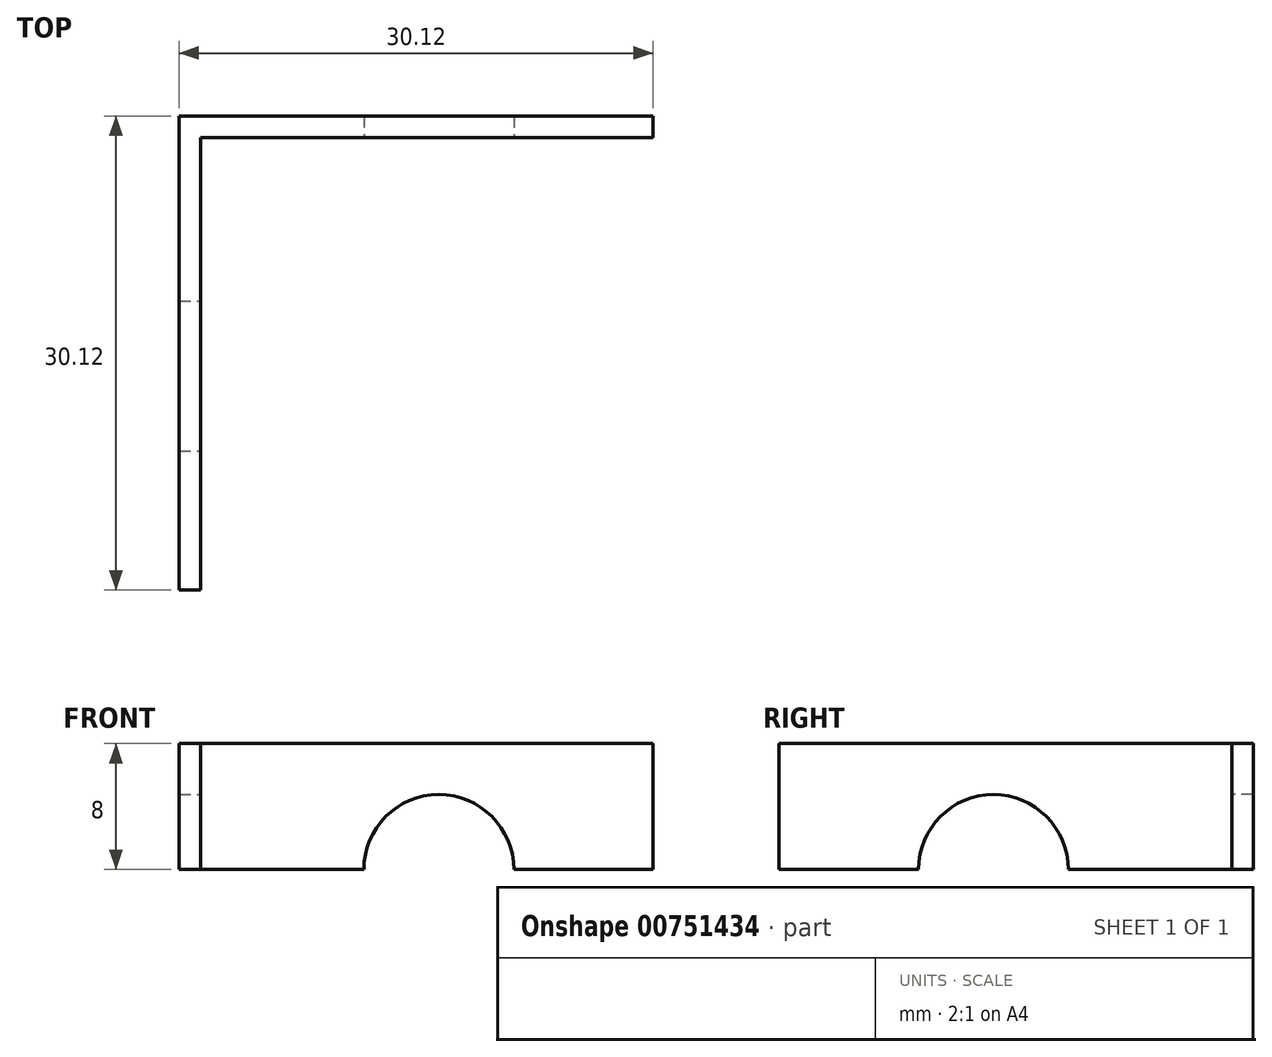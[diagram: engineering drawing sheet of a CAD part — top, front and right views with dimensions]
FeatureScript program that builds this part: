
annotation { "Feature Type Name" : "Feature", "Feature Type Description" : "" }
export const myFeature = defineFeature(function(context is Context, id is Id, definition is map)
    precondition{}
    {
        {
            assignVariable(context, id + "F0", {"name" : "height", "anyValue" : 8});
        }
        {
            var Q0;
            Q0=qCreatedBy(makeId("Top.planeOp"),FACE);
            var sketch = newSketch(context, id + "F1", { "sketchPlane" : qUnion([Q0])});
            skLineSegment(sketch, "E0", {"start": v(-1.37, -28.75) * mm, "end": v(-1.37, 1.37) * mm});
            skLineSegment(sketch, "E1", {"start": v(-1.37, 1.37) * mm, "end": v(28.75, 1.37) * mm});
            skLineSegment(sketch, "E2", {"start": v(28.75, 1.37) * mm, "end": v(28.75, 0) * mm});
            skLineSegment(sketch, "E3", {"start": v(28.75, 0) * mm, "end": v(0, 0) * mm});
            skLineSegment(sketch, "E4", {"start": v(0, 0) * mm, "end": v(0, -28.75) * mm});
            skLineSegment(sketch, "E5", {"start": v(0, -28.75) * mm, "end": v(-1.37, -28.75) * mm});
            skSolve(sketch);
        }
        {
            var Q0;
            Q0=makeQuery(id+"F1.imprint","IMPRINT",FACE,{"disambiguationData":[TD([[makeQuery(id+"F1.imprint","IMPRINT",EDGE,{"derivedFrom":sQuery(id+"F1.wireOp",EDGE,"E0")}),-1.0]])]});
            extrude(context, id + "F2", {"entities" : qUnion([Q0]), "depth" : (getVariable(context, 'height')) * mm, "offsetDistance" : 25.4 * mm});
        }
        {
            var Q0;
            Q0=makeQuery(id+"F2.opExtrude","SWEPT_FACE",FACE,{"disambiguationData":[OSD([sQuery(id+"F1.wireOp",EDGE,"E3")])]});
            var sketch = newSketch(context, id + "F3", { "sketchPlane" : qUnion([Q0])});
            skPoint(sketch, "E6", {"position": v(15.14, 19.05) * mm});
            skLineSegment(sketch, "E7", {"start": v(15.14, 0) * mm, "end": v(15.14, 203.2) * mm, "construction": true});
            skCircle(sketch, "E8", {"center": v(15.14, 19.05) * mm, "radius": 4.76 * mm});
            skCircle(sketch, "E9", {"center": v(15.14, 0) * mm, "radius": 4.76 * mm});
            skPoint(sketch, "E10", {"position": v(15.14, 38.1) * mm});
            skPoint(sketch, "E11", {"position": v(15.14, 57.15) * mm});
            skArc(sketch, "E12", {"start": v(19.9, 39.69) * mm, "mid": v(15.14, 44.45) * mm, "end": v(10.38, 39.69) * mm});
            skArc(sketch, "E13", {"start": v(10.38, 36.51) * mm, "mid": v(15.14, 31.75) * mm, "end": v(19.9, 36.51) * mm});
            skLineSegment(sketch, "E14", {"start": v(19.9, 39.69) * mm, "end": v(19.9, 36.51) * mm});
            skLineSegment(sketch, "E15", {"start": v(10.38, 39.69) * mm, "end": v(10.38, 36.51) * mm});
            skArc(sketch, "E16", {"start": v(19.9, 58.74) * mm, "mid": v(15.14, 63.5) * mm, "end": v(10.38, 58.74) * mm});
            skArc(sketch, "E17", {"start": v(10.38, 55.56) * mm, "mid": v(15.14, 50.8) * mm, "end": v(19.9, 55.56) * mm});
            skLineSegment(sketch, "E18", {"start": v(19.9, 58.74) * mm, "end": v(19.9, 55.56) * mm});
            skLineSegment(sketch, "E19", {"start": v(10.38, 58.74) * mm, "end": v(10.38, 55.56) * mm});
            skPoint(sketch, "E20.0.1.0", {"position": v(15.14, 133.35) * mm});
            skArc(sketch, "E20.0.1.1", {"start": v(19.9, 134.94) * mm, "mid": v(15.14, 139.7) * mm, "end": v(10.38, 134.94) * mm});
            skPoint(sketch, "E20.0.1.2", {"position": v(15.14, 114.3) * mm});
            skPoint(sketch, "E20.0.1.3", {"position": v(15.14, 95.25) * mm});
            skArc(sketch, "E20.0.1.4", {"start": v(10.38, 131.76) * mm, "mid": v(15.14, 127) * mm, "end": v(19.9, 131.76) * mm});
            skCircle(sketch, "E20.0.1.5", {"center": v(15.14, 95.25) * mm, "radius": 4.76 * mm});
            skCircle(sketch, "E20.0.1.6", {"center": v(15.14, 76.2) * mm, "radius": 4.76 * mm});
            skArc(sketch, "E20.0.1.7", {"start": v(19.9, 115.89) * mm, "mid": v(15.14, 120.65) * mm, "end": v(10.38, 115.89) * mm});
            skArc(sketch, "E20.0.1.8", {"start": v(10.38, 112.71) * mm, "mid": v(15.14, 107.95) * mm, "end": v(19.9, 112.71) * mm});
            skPoint(sketch, "E20.0.1.9", {"position": v(15.14, 133.35) * mm});
            skPoint(sketch, "E20.0.1.10", {"position": v(15.14, 114.3) * mm});
            skLineSegment(sketch, "E20.0.1.11", {"start": v(10.38, 134.94) * mm, "end": v(10.38, 131.76) * mm});
            skLineSegment(sketch, "E20.0.1.12", {"start": v(19.9, 134.94) * mm, "end": v(19.9, 131.76) * mm});
            skLineSegment(sketch, "E20.0.1.13", {"start": v(19.9, 115.89) * mm, "end": v(19.9, 112.71) * mm});
            skLineSegment(sketch, "E20.0.1.14", {"start": v(10.38, 115.89) * mm, "end": v(10.38, 112.71) * mm});
            skPoint(sketch, "E20.0.2.0", {"position": v(15.14, 209.55) * mm});
            skArc(sketch, "E20.0.2.1", {"start": v(19.9, 211.14) * mm, "mid": v(15.14, 215.9) * mm, "end": v(10.38, 211.14) * mm});
            skPoint(sketch, "E20.0.2.2", {"position": v(15.14, 190.5) * mm});
            skPoint(sketch, "E20.0.2.3", {"position": v(15.14, 171.45) * mm});
            skArc(sketch, "E20.0.2.4", {"start": v(10.38, 207.96) * mm, "mid": v(15.14, 203.2) * mm, "end": v(19.9, 207.96) * mm});
            skCircle(sketch, "E20.0.2.5", {"center": v(15.14, 171.45) * mm, "radius": 4.76 * mm});
            skCircle(sketch, "E20.0.2.6", {"center": v(15.14, 152.4) * mm, "radius": 4.76 * mm});
            skArc(sketch, "E20.0.2.7", {"start": v(19.9, 192.09) * mm, "mid": v(15.14, 196.85) * mm, "end": v(10.38, 192.09) * mm});
            skArc(sketch, "E20.0.2.8", {"start": v(10.38, 188.91) * mm, "mid": v(15.14, 184.15) * mm, "end": v(19.9, 188.91) * mm});
            skPoint(sketch, "E20.0.2.9", {"position": v(15.14, 209.55) * mm});
            skPoint(sketch, "E20.0.2.10", {"position": v(15.14, 190.5) * mm});
            skLineSegment(sketch, "E20.0.2.11", {"start": v(10.38, 211.14) * mm, "end": v(10.38, 207.96) * mm});
            skLineSegment(sketch, "E20.0.2.12", {"start": v(19.9, 211.14) * mm, "end": v(19.9, 207.96) * mm});
            skLineSegment(sketch, "E20.0.2.13", {"start": v(19.9, 192.09) * mm, "end": v(19.9, 188.91) * mm});
            skLineSegment(sketch, "E20.0.2.14", {"start": v(10.38, 192.09) * mm, "end": v(10.38, 188.91) * mm});
            skPoint(sketch, "E20.0.3.0", {"position": v(15.14, 285.75) * mm});
            skArc(sketch, "E20.0.3.1", {"start": v(19.9, 287.34) * mm, "mid": v(15.14, 292.1) * mm, "end": v(10.38, 287.34) * mm});
            skPoint(sketch, "E20.0.3.2", {"position": v(15.14, 266.7) * mm});
            skPoint(sketch, "E20.0.3.3", {"position": v(15.14, 247.65) * mm});
            skArc(sketch, "E20.0.3.4", {"start": v(10.38, 284.16) * mm, "mid": v(15.14, 279.4) * mm, "end": v(19.9, 284.16) * mm});
            skCircle(sketch, "E20.0.3.5", {"center": v(15.14, 247.65) * mm, "radius": 4.76 * mm});
            skCircle(sketch, "E20.0.3.6", {"center": v(15.14, 228.6) * mm, "radius": 4.76 * mm});
            skArc(sketch, "E20.0.3.7", {"start": v(19.9, 268.29) * mm, "mid": v(15.14, 273.05) * mm, "end": v(10.38, 268.29) * mm});
            skArc(sketch, "E20.0.3.8", {"start": v(10.38, 265.11) * mm, "mid": v(15.14, 260.35) * mm, "end": v(19.9, 265.11) * mm});
            skPoint(sketch, "E20.0.3.9", {"position": v(15.14, 285.75) * mm});
            skPoint(sketch, "E20.0.3.10", {"position": v(15.14, 266.7) * mm});
            skLineSegment(sketch, "E20.0.3.11", {"start": v(10.38, 287.34) * mm, "end": v(10.38, 284.16) * mm});
            skLineSegment(sketch, "E20.0.3.12", {"start": v(19.9, 287.34) * mm, "end": v(19.9, 284.16) * mm});
            skLineSegment(sketch, "E20.0.3.13", {"start": v(19.9, 268.29) * mm, "end": v(19.9, 265.11) * mm});
            skLineSegment(sketch, "E20.0.3.14", {"start": v(10.38, 268.29) * mm, "end": v(10.38, 265.11) * mm});
            skPoint(sketch, "E20.0.4.0", {"position": v(15.14, 361.95) * mm});
            skArc(sketch, "E20.0.4.1", {"start": v(19.9, 363.54) * mm, "mid": v(15.14, 368.3) * mm, "end": v(10.38, 363.54) * mm});
            skPoint(sketch, "E20.0.4.2", {"position": v(15.14, 342.9) * mm});
            skPoint(sketch, "E20.0.4.3", {"position": v(15.14, 323.85) * mm});
            skArc(sketch, "E20.0.4.4", {"start": v(10.38, 360.36) * mm, "mid": v(15.14, 355.6) * mm, "end": v(19.9, 360.36) * mm});
            skCircle(sketch, "E20.0.4.5", {"center": v(15.14, 323.85) * mm, "radius": 4.76 * mm});
            skCircle(sketch, "E20.0.4.6", {"center": v(15.14, 304.8) * mm, "radius": 4.76 * mm});
            skArc(sketch, "E20.0.4.7", {"start": v(19.9, 344.49) * mm, "mid": v(15.14, 349.25) * mm, "end": v(10.38, 344.49) * mm});
            skArc(sketch, "E20.0.4.8", {"start": v(10.38, 341.31) * mm, "mid": v(15.14, 336.55) * mm, "end": v(19.9, 341.31) * mm});
            skPoint(sketch, "E20.0.4.9", {"position": v(15.14, 361.95) * mm});
            skPoint(sketch, "E20.0.4.10", {"position": v(15.14, 342.9) * mm});
            skLineSegment(sketch, "E20.0.4.11", {"start": v(10.38, 363.54) * mm, "end": v(10.38, 360.36) * mm});
            skLineSegment(sketch, "E20.0.4.12", {"start": v(19.9, 363.54) * mm, "end": v(19.9, 360.36) * mm});
            skLineSegment(sketch, "E20.0.4.13", {"start": v(19.9, 344.49) * mm, "end": v(19.9, 341.31) * mm});
            skLineSegment(sketch, "E20.0.4.14", {"start": v(10.38, 344.49) * mm, "end": v(10.38, 341.31) * mm});
            skPoint(sketch, "E20.0.5.0", {"position": v(15.14, 438.15) * mm});
            skArc(sketch, "E20.0.5.1", {"start": v(19.9, 439.74) * mm, "mid": v(15.14, 444.5) * mm, "end": v(10.38, 439.74) * mm});
            skPoint(sketch, "E20.0.5.2", {"position": v(15.14, 419.1) * mm});
            skPoint(sketch, "E20.0.5.3", {"position": v(15.14, 400.05) * mm});
            skArc(sketch, "E20.0.5.4", {"start": v(10.38, 436.56) * mm, "mid": v(15.14, 431.8) * mm, "end": v(19.9, 436.56) * mm});
            skCircle(sketch, "E20.0.5.5", {"center": v(15.14, 400.05) * mm, "radius": 4.76 * mm});
            skCircle(sketch, "E20.0.5.6", {"center": v(15.14, 381) * mm, "radius": 4.76 * mm});
            skArc(sketch, "E20.0.5.7", {"start": v(19.9, 420.69) * mm, "mid": v(15.14, 425.45) * mm, "end": v(10.38, 420.69) * mm});
            skArc(sketch, "E20.0.5.8", {"start": v(10.38, 417.51) * mm, "mid": v(15.14, 412.75) * mm, "end": v(19.9, 417.51) * mm});
            skPoint(sketch, "E20.0.5.9", {"position": v(15.14, 438.15) * mm});
            skPoint(sketch, "E20.0.5.10", {"position": v(15.14, 419.1) * mm});
            skLineSegment(sketch, "E20.0.5.11", {"start": v(10.38, 439.74) * mm, "end": v(10.38, 436.56) * mm});
            skLineSegment(sketch, "E20.0.5.12", {"start": v(19.9, 439.74) * mm, "end": v(19.9, 436.56) * mm});
            skLineSegment(sketch, "E20.0.5.13", {"start": v(19.9, 420.69) * mm, "end": v(19.9, 417.51) * mm});
            skLineSegment(sketch, "E20.0.5.14", {"start": v(10.38, 420.69) * mm, "end": v(10.38, 417.51) * mm});
            skPoint(sketch, "E20.0.6.0", {"position": v(15.14, 514.35) * mm});
            skArc(sketch, "E20.0.6.1", {"start": v(19.9, 515.94) * mm, "mid": v(15.14, 520.7) * mm, "end": v(10.38, 515.94) * mm});
            skPoint(sketch, "E20.0.6.2", {"position": v(15.14, 495.3) * mm});
            skPoint(sketch, "E20.0.6.3", {"position": v(15.14, 476.25) * mm});
            skArc(sketch, "E20.0.6.4", {"start": v(10.38, 512.76) * mm, "mid": v(15.14, 508) * mm, "end": v(19.9, 512.76) * mm});
            skCircle(sketch, "E20.0.6.5", {"center": v(15.14, 476.25) * mm, "radius": 4.76 * mm});
            skCircle(sketch, "E20.0.6.6", {"center": v(15.14, 457.2) * mm, "radius": 4.76 * mm});
            skArc(sketch, "E20.0.6.7", {"start": v(19.9, 496.89) * mm, "mid": v(15.14, 501.65) * mm, "end": v(10.38, 496.89) * mm});
            skArc(sketch, "E20.0.6.8", {"start": v(10.38, 493.71) * mm, "mid": v(15.14, 488.95) * mm, "end": v(19.9, 493.71) * mm});
            skPoint(sketch, "E20.0.6.9", {"position": v(15.14, 514.35) * mm});
            skPoint(sketch, "E20.0.6.10", {"position": v(15.14, 495.3) * mm});
            skLineSegment(sketch, "E20.0.6.11", {"start": v(10.38, 515.94) * mm, "end": v(10.38, 512.76) * mm});
            skLineSegment(sketch, "E20.0.6.12", {"start": v(19.9, 515.94) * mm, "end": v(19.9, 512.76) * mm});
            skLineSegment(sketch, "E20.0.6.13", {"start": v(19.9, 496.89) * mm, "end": v(19.9, 493.71) * mm});
            skLineSegment(sketch, "E20.0.6.14", {"start": v(10.38, 496.89) * mm, "end": v(10.38, 493.71) * mm});
            skPoint(sketch, "E20.0.7.0", {"position": v(15.14, 590.55) * mm});
            skArc(sketch, "E20.0.7.1", {"start": v(19.9, 592.14) * mm, "mid": v(15.14, 596.9) * mm, "end": v(10.38, 592.14) * mm});
            skPoint(sketch, "E20.0.7.2", {"position": v(15.14, 571.5) * mm});
            skPoint(sketch, "E20.0.7.3", {"position": v(15.14, 552.45) * mm});
            skArc(sketch, "E20.0.7.4", {"start": v(10.38, 588.96) * mm, "mid": v(15.14, 584.2) * mm, "end": v(19.9, 588.96) * mm});
            skCircle(sketch, "E20.0.7.5", {"center": v(15.14, 552.45) * mm, "radius": 4.76 * mm});
            skCircle(sketch, "E20.0.7.6", {"center": v(15.14, 533.4) * mm, "radius": 4.76 * mm});
            skArc(sketch, "E20.0.7.7", {"start": v(19.9, 573.09) * mm, "mid": v(15.14, 577.85) * mm, "end": v(10.38, 573.09) * mm});
            skArc(sketch, "E20.0.7.8", {"start": v(10.38, 569.91) * mm, "mid": v(15.14, 565.15) * mm, "end": v(19.9, 569.91) * mm});
            skPoint(sketch, "E20.0.7.9", {"position": v(15.14, 590.55) * mm});
            skPoint(sketch, "E20.0.7.10", {"position": v(15.14, 571.5) * mm});
            skLineSegment(sketch, "E20.0.7.11", {"start": v(10.38, 592.14) * mm, "end": v(10.38, 588.96) * mm});
            skLineSegment(sketch, "E20.0.7.12", {"start": v(19.9, 592.14) * mm, "end": v(19.9, 588.96) * mm});
            skLineSegment(sketch, "E20.0.7.13", {"start": v(19.9, 573.09) * mm, "end": v(19.9, 569.91) * mm});
            skLineSegment(sketch, "E20.0.7.14", {"start": v(10.38, 573.09) * mm, "end": v(10.38, 569.91) * mm});
            skPoint(sketch, "E20.0.8.0", {"position": v(15.14, 666.75) * mm});
            skArc(sketch, "E20.0.8.1", {"start": v(19.9, 668.34) * mm, "mid": v(15.14, 673.1) * mm, "end": v(10.38, 668.34) * mm});
            skPoint(sketch, "E20.0.8.2", {"position": v(15.14, 647.7) * mm});
            skPoint(sketch, "E20.0.8.3", {"position": v(15.14, 628.65) * mm});
            skArc(sketch, "E20.0.8.4", {"start": v(10.38, 665.16) * mm, "mid": v(15.14, 660.4) * mm, "end": v(19.9, 665.16) * mm});
            skCircle(sketch, "E20.0.8.5", {"center": v(15.14, 628.65) * mm, "radius": 4.76 * mm});
            skCircle(sketch, "E20.0.8.6", {"center": v(15.14, 609.6) * mm, "radius": 4.76 * mm});
            skArc(sketch, "E20.0.8.7", {"start": v(19.9, 649.29) * mm, "mid": v(15.14, 654.05) * mm, "end": v(10.38, 649.29) * mm});
            skArc(sketch, "E20.0.8.8", {"start": v(10.38, 646.11) * mm, "mid": v(15.14, 641.35) * mm, "end": v(19.9, 646.11) * mm});
            skPoint(sketch, "E20.0.8.9", {"position": v(15.14, 666.75) * mm});
            skPoint(sketch, "E20.0.8.10", {"position": v(15.14, 647.7) * mm});
            skLineSegment(sketch, "E20.0.8.11", {"start": v(10.38, 668.34) * mm, "end": v(10.38, 665.16) * mm});
            skLineSegment(sketch, "E20.0.8.12", {"start": v(19.9, 668.34) * mm, "end": v(19.9, 665.16) * mm});
            skLineSegment(sketch, "E20.0.8.13", {"start": v(19.9, 649.29) * mm, "end": v(19.9, 646.11) * mm});
            skLineSegment(sketch, "E20.0.8.14", {"start": v(10.38, 649.29) * mm, "end": v(10.38, 646.11) * mm});
            skPoint(sketch, "E20.0.9.0", {"position": v(15.14, 742.95) * mm});
            skArc(sketch, "E20.0.9.1", {"start": v(19.9, 744.54) * mm, "mid": v(15.14, 749.3) * mm, "end": v(10.38, 744.54) * mm});
            skPoint(sketch, "E20.0.9.2", {"position": v(15.14, 723.9) * mm});
            skPoint(sketch, "E20.0.9.3", {"position": v(15.14, 704.85) * mm});
            skArc(sketch, "E20.0.9.4", {"start": v(10.38, 741.36) * mm, "mid": v(15.14, 736.6) * mm, "end": v(19.9, 741.36) * mm});
            skCircle(sketch, "E20.0.9.5", {"center": v(15.14, 704.85) * mm, "radius": 4.76 * mm});
            skCircle(sketch, "E20.0.9.6", {"center": v(15.14, 685.8) * mm, "radius": 4.76 * mm});
            skArc(sketch, "E20.0.9.7", {"start": v(19.9, 725.49) * mm, "mid": v(15.14, 730.25) * mm, "end": v(10.38, 725.49) * mm});
            skArc(sketch, "E20.0.9.8", {"start": v(10.38, 722.31) * mm, "mid": v(15.14, 717.55) * mm, "end": v(19.9, 722.31) * mm});
            skPoint(sketch, "E20.0.9.9", {"position": v(15.14, 742.95) * mm});
            skPoint(sketch, "E20.0.9.10", {"position": v(15.14, 723.9) * mm});
            skLineSegment(sketch, "E20.0.9.11", {"start": v(10.38, 744.54) * mm, "end": v(10.38, 741.36) * mm});
            skLineSegment(sketch, "E20.0.9.12", {"start": v(19.9, 744.54) * mm, "end": v(19.9, 741.36) * mm});
            skLineSegment(sketch, "E20.0.9.13", {"start": v(19.9, 725.49) * mm, "end": v(19.9, 722.31) * mm});
            skLineSegment(sketch, "E20.0.9.14", {"start": v(10.38, 725.49) * mm, "end": v(10.38, 722.31) * mm});
            skPoint(sketch, "E20.0.10.0", {"position": v(15.14, 819.15) * mm});
            skArc(sketch, "E20.0.10.1", {"start": v(19.9, 820.74) * mm, "mid": v(15.14, 825.5) * mm, "end": v(10.38, 820.74) * mm});
            skPoint(sketch, "E20.0.10.2", {"position": v(15.14, 800.1) * mm});
            skPoint(sketch, "E20.0.10.3", {"position": v(15.14, 781.05) * mm});
            skArc(sketch, "E20.0.10.4", {"start": v(10.38, 817.56) * mm, "mid": v(15.14, 812.8) * mm, "end": v(19.9, 817.56) * mm});
            skCircle(sketch, "E20.0.10.5", {"center": v(15.14, 781.05) * mm, "radius": 4.76 * mm});
            skCircle(sketch, "E20.0.10.6", {"center": v(15.14, 762) * mm, "radius": 4.76 * mm});
            skArc(sketch, "E20.0.10.7", {"start": v(19.9, 801.69) * mm, "mid": v(15.14, 806.45) * mm, "end": v(10.38, 801.69) * mm});
            skArc(sketch, "E20.0.10.8", {"start": v(10.38, 798.51) * mm, "mid": v(15.14, 793.75) * mm, "end": v(19.9, 798.51) * mm});
            skPoint(sketch, "E20.0.10.9", {"position": v(15.14, 819.15) * mm});
            skPoint(sketch, "E20.0.10.10", {"position": v(15.14, 800.1) * mm});
            skLineSegment(sketch, "E20.0.10.11", {"start": v(10.38, 820.74) * mm, "end": v(10.38, 817.56) * mm});
            skLineSegment(sketch, "E20.0.10.12", {"start": v(19.9, 820.74) * mm, "end": v(19.9, 817.56) * mm});
            skLineSegment(sketch, "E20.0.10.13", {"start": v(19.9, 801.69) * mm, "end": v(19.9, 798.51) * mm});
            skLineSegment(sketch, "E20.0.10.14", {"start": v(10.38, 801.69) * mm, "end": v(10.38, 798.51) * mm});
            skPoint(sketch, "E20.0.11.0", {"position": v(15.14, 895.35) * mm});
            skArc(sketch, "E20.0.11.1", {"start": v(19.9, 896.94) * mm, "mid": v(15.14, 901.7) * mm, "end": v(10.38, 896.94) * mm});
            skPoint(sketch, "E20.0.11.2", {"position": v(15.14, 876.3) * mm});
            skPoint(sketch, "E20.0.11.3", {"position": v(15.14, 857.25) * mm});
            skArc(sketch, "E20.0.11.4", {"start": v(10.38, 893.76) * mm, "mid": v(15.14, 889) * mm, "end": v(19.9, 893.76) * mm});
            skCircle(sketch, "E20.0.11.5", {"center": v(15.14, 857.25) * mm, "radius": 4.76 * mm});
            skCircle(sketch, "E20.0.11.6", {"center": v(15.14, 838.2) * mm, "radius": 4.76 * mm});
            skArc(sketch, "E20.0.11.7", {"start": v(19.9, 877.89) * mm, "mid": v(15.14, 882.65) * mm, "end": v(10.38, 877.89) * mm});
            skArc(sketch, "E20.0.11.8", {"start": v(10.38, 874.71) * mm, "mid": v(15.14, 869.95) * mm, "end": v(19.9, 874.71) * mm});
            skPoint(sketch, "E20.0.11.9", {"position": v(15.14, 895.35) * mm});
            skPoint(sketch, "E20.0.11.10", {"position": v(15.14, 876.3) * mm});
            skLineSegment(sketch, "E20.0.11.11", {"start": v(10.38, 896.94) * mm, "end": v(10.38, 893.76) * mm});
            skLineSegment(sketch, "E20.0.11.12", {"start": v(19.9, 896.94) * mm, "end": v(19.9, 893.76) * mm});
            skLineSegment(sketch, "E20.0.11.13", {"start": v(19.9, 877.89) * mm, "end": v(19.9, 874.71) * mm});
            skLineSegment(sketch, "E20.0.11.14", {"start": v(10.38, 877.89) * mm, "end": v(10.38, 874.71) * mm});
            skPoint(sketch, "E20.0.12.0", {"position": v(15.14, 971.55) * mm});
            skArc(sketch, "E20.0.12.1", {"start": v(19.9, 973.14) * mm, "mid": v(15.14, 977.9) * mm, "end": v(10.38, 973.14) * mm});
            skPoint(sketch, "E20.0.12.2", {"position": v(15.14, 952.5) * mm});
            skPoint(sketch, "E20.0.12.3", {"position": v(15.14, 933.45) * mm});
            skArc(sketch, "E20.0.12.4", {"start": v(10.38, 969.96) * mm, "mid": v(15.14, 965.2) * mm, "end": v(19.9, 969.96) * mm});
            skCircle(sketch, "E20.0.12.5", {"center": v(15.14, 933.45) * mm, "radius": 4.76 * mm});
            skCircle(sketch, "E20.0.12.6", {"center": v(15.14, 914.4) * mm, "radius": 4.76 * mm});
            skArc(sketch, "E20.0.12.7", {"start": v(19.9, 954.09) * mm, "mid": v(15.14, 958.85) * mm, "end": v(10.38, 954.09) * mm});
            skArc(sketch, "E20.0.12.8", {"start": v(10.38, 950.91) * mm, "mid": v(15.14, 946.15) * mm, "end": v(19.9, 950.91) * mm});
            skPoint(sketch, "E20.0.12.9", {"position": v(15.14, 971.55) * mm});
            skPoint(sketch, "E20.0.12.10", {"position": v(15.14, 952.5) * mm});
            skLineSegment(sketch, "E20.0.12.11", {"start": v(10.38, 973.14) * mm, "end": v(10.38, 969.96) * mm});
            skLineSegment(sketch, "E20.0.12.12", {"start": v(19.9, 973.14) * mm, "end": v(19.9, 969.96) * mm});
            skLineSegment(sketch, "E20.0.12.13", {"start": v(19.9, 954.09) * mm, "end": v(19.9, 950.91) * mm});
            skLineSegment(sketch, "E20.0.12.14", {"start": v(10.38, 954.09) * mm, "end": v(10.38, 950.91) * mm});
            skPoint(sketch, "E20.0.13.0", {"position": v(15.14, 1047.75) * mm});
            skArc(sketch, "E20.0.13.1", {"start": v(19.9, 1049.34) * mm, "mid": v(15.14, 1054.1) * mm, "end": v(10.38, 1049.34) * mm});
            skPoint(sketch, "E20.0.13.2", {"position": v(15.14, 1028.7) * mm});
            skPoint(sketch, "E20.0.13.3", {"position": v(15.14, 1009.65) * mm});
            skArc(sketch, "E20.0.13.4", {"start": v(10.38, 1046.16) * mm, "mid": v(15.14, 1041.4) * mm, "end": v(19.9, 1046.16) * mm});
            skCircle(sketch, "E20.0.13.5", {"center": v(15.14, 1009.65) * mm, "radius": 4.76 * mm});
            skCircle(sketch, "E20.0.13.6", {"center": v(15.14, 990.6) * mm, "radius": 4.76 * mm});
            skArc(sketch, "E20.0.13.7", {"start": v(19.9, 1030.29) * mm, "mid": v(15.14, 1035.05) * mm, "end": v(10.38, 1030.29) * mm});
            skArc(sketch, "E20.0.13.8", {"start": v(10.38, 1027.11) * mm, "mid": v(15.14, 1022.35) * mm, "end": v(19.9, 1027.11) * mm});
            skPoint(sketch, "E20.0.13.9", {"position": v(15.14, 1047.75) * mm});
            skPoint(sketch, "E20.0.13.10", {"position": v(15.14, 1028.7) * mm});
            skLineSegment(sketch, "E20.0.13.11", {"start": v(10.38, 1049.34) * mm, "end": v(10.38, 1046.16) * mm});
            skLineSegment(sketch, "E20.0.13.12", {"start": v(19.9, 1049.34) * mm, "end": v(19.9, 1046.16) * mm});
            skLineSegment(sketch, "E20.0.13.13", {"start": v(19.9, 1030.29) * mm, "end": v(19.9, 1027.11) * mm});
            skLineSegment(sketch, "E20.0.13.14", {"start": v(10.38, 1030.29) * mm, "end": v(10.38, 1027.11) * mm});
            skPoint(sketch, "E20.0.14.0", {"position": v(15.14, 1123.95) * mm});
            skArc(sketch, "E20.0.14.1", {"start": v(19.9, 1125.54) * mm, "mid": v(15.14, 1130.3) * mm, "end": v(10.38, 1125.54) * mm});
            skPoint(sketch, "E20.0.14.2", {"position": v(15.14, 1104.9) * mm});
            skPoint(sketch, "E20.0.14.3", {"position": v(15.14, 1085.85) * mm});
            skArc(sketch, "E20.0.14.4", {"start": v(10.38, 1122.36) * mm, "mid": v(15.14, 1117.6) * mm, "end": v(19.9, 1122.36) * mm});
            skCircle(sketch, "E20.0.14.5", {"center": v(15.14, 1085.85) * mm, "radius": 4.76 * mm});
            skCircle(sketch, "E20.0.14.6", {"center": v(15.14, 1066.8) * mm, "radius": 4.76 * mm});
            skArc(sketch, "E20.0.14.7", {"start": v(19.9, 1106.49) * mm, "mid": v(15.14, 1111.25) * mm, "end": v(10.38, 1106.49) * mm});
            skArc(sketch, "E20.0.14.8", {"start": v(10.38, 1103.31) * mm, "mid": v(15.14, 1098.55) * mm, "end": v(19.9, 1103.31) * mm});
            skPoint(sketch, "E20.0.14.9", {"position": v(15.14, 1123.95) * mm});
            skPoint(sketch, "E20.0.14.10", {"position": v(15.14, 1104.9) * mm});
            skLineSegment(sketch, "E20.0.14.11", {"start": v(10.38, 1125.54) * mm, "end": v(10.38, 1122.36) * mm});
            skLineSegment(sketch, "E20.0.14.12", {"start": v(19.9, 1125.54) * mm, "end": v(19.9, 1122.36) * mm});
            skLineSegment(sketch, "E20.0.14.13", {"start": v(19.9, 1106.49) * mm, "end": v(19.9, 1103.31) * mm});
            skLineSegment(sketch, "E20.0.14.14", {"start": v(10.38, 1106.49) * mm, "end": v(10.38, 1103.31) * mm});
            skPoint(sketch, "E20.0.15.0", {"position": v(15.14, 1200.15) * mm});
            skArc(sketch, "E20.0.15.1", {"start": v(19.9, 1201.74) * mm, "mid": v(15.14, 1206.5) * mm, "end": v(10.38, 1201.74) * mm});
            skPoint(sketch, "E20.0.15.2", {"position": v(15.14, 1181.1) * mm});
            skPoint(sketch, "E20.0.15.3", {"position": v(15.14, 1162.05) * mm});
            skArc(sketch, "E20.0.15.4", {"start": v(10.38, 1198.56) * mm, "mid": v(15.14, 1193.8) * mm, "end": v(19.9, 1198.56) * mm});
            skCircle(sketch, "E20.0.15.5", {"center": v(15.14, 1162.05) * mm, "radius": 4.76 * mm});
            skCircle(sketch, "E20.0.15.6", {"center": v(15.14, 1143) * mm, "radius": 4.76 * mm});
            skArc(sketch, "E20.0.15.7", {"start": v(19.9, 1182.69) * mm, "mid": v(15.14, 1187.45) * mm, "end": v(10.38, 1182.69) * mm});
            skArc(sketch, "E20.0.15.8", {"start": v(10.38, 1179.51) * mm, "mid": v(15.14, 1174.75) * mm, "end": v(19.9, 1179.51) * mm});
            skPoint(sketch, "E20.0.15.9", {"position": v(15.14, 1200.15) * mm});
            skPoint(sketch, "E20.0.15.10", {"position": v(15.14, 1181.1) * mm});
            skLineSegment(sketch, "E20.0.15.11", {"start": v(10.38, 1201.74) * mm, "end": v(10.38, 1198.56) * mm});
            skLineSegment(sketch, "E20.0.15.12", {"start": v(19.9, 1201.74) * mm, "end": v(19.9, 1198.56) * mm});
            skLineSegment(sketch, "E20.0.15.13", {"start": v(19.9, 1182.69) * mm, "end": v(19.9, 1179.51) * mm});
            skLineSegment(sketch, "E20.0.15.14", {"start": v(10.38, 1182.69) * mm, "end": v(10.38, 1179.51) * mm});
            skPoint(sketch, "E20.0.16.0", {"position": v(15.14, 1276.35) * mm});
            skArc(sketch, "E20.0.16.1", {"start": v(19.9, 1277.94) * mm, "mid": v(15.14, 1282.7) * mm, "end": v(10.38, 1277.94) * mm});
            skPoint(sketch, "E20.0.16.2", {"position": v(15.14, 1257.3) * mm});
            skPoint(sketch, "E20.0.16.3", {"position": v(15.14, 1238.25) * mm});
            skArc(sketch, "E20.0.16.4", {"start": v(10.38, 1274.76) * mm, "mid": v(15.14, 1270) * mm, "end": v(19.9, 1274.76) * mm});
            skCircle(sketch, "E20.0.16.5", {"center": v(15.14, 1238.25) * mm, "radius": 4.76 * mm});
            skCircle(sketch, "E20.0.16.6", {"center": v(15.14, 1219.2) * mm, "radius": 4.76 * mm});
            skArc(sketch, "E20.0.16.7", {"start": v(19.9, 1258.89) * mm, "mid": v(15.14, 1263.65) * mm, "end": v(10.38, 1258.89) * mm});
            skArc(sketch, "E20.0.16.8", {"start": v(10.38, 1255.71) * mm, "mid": v(15.14, 1250.95) * mm, "end": v(19.9, 1255.71) * mm});
            skPoint(sketch, "E20.0.16.9", {"position": v(15.14, 1276.35) * mm});
            skPoint(sketch, "E20.0.16.10", {"position": v(15.14, 1257.3) * mm});
            skLineSegment(sketch, "E20.0.16.11", {"start": v(10.38, 1277.94) * mm, "end": v(10.38, 1274.76) * mm});
            skLineSegment(sketch, "E20.0.16.12", {"start": v(19.9, 1277.94) * mm, "end": v(19.9, 1274.76) * mm});
            skLineSegment(sketch, "E20.0.16.13", {"start": v(19.9, 1258.89) * mm, "end": v(19.9, 1255.71) * mm});
            skLineSegment(sketch, "E20.0.16.14", {"start": v(10.38, 1258.89) * mm, "end": v(10.38, 1255.71) * mm});
            skPoint(sketch, "E20.0.17.0", {"position": v(15.14, 1352.55) * mm});
            skArc(sketch, "E20.0.17.1", {"start": v(19.9, 1354.14) * mm, "mid": v(15.14, 1358.9) * mm, "end": v(10.38, 1354.14) * mm});
            skPoint(sketch, "E20.0.17.2", {"position": v(15.14, 1333.5) * mm});
            skPoint(sketch, "E20.0.17.3", {"position": v(15.14, 1314.45) * mm});
            skArc(sketch, "E20.0.17.4", {"start": v(10.38, 1350.96) * mm, "mid": v(15.14, 1346.2) * mm, "end": v(19.9, 1350.96) * mm});
            skCircle(sketch, "E20.0.17.5", {"center": v(15.14, 1314.45) * mm, "radius": 4.76 * mm});
            skCircle(sketch, "E20.0.17.6", {"center": v(15.14, 1295.4) * mm, "radius": 4.76 * mm});
            skArc(sketch, "E20.0.17.7", {"start": v(19.9, 1335.09) * mm, "mid": v(15.14, 1339.85) * mm, "end": v(10.38, 1335.09) * mm});
            skArc(sketch, "E20.0.17.8", {"start": v(10.38, 1331.91) * mm, "mid": v(15.14, 1327.15) * mm, "end": v(19.9, 1331.91) * mm});
            skPoint(sketch, "E20.0.17.9", {"position": v(15.14, 1352.55) * mm});
            skPoint(sketch, "E20.0.17.10", {"position": v(15.14, 1333.5) * mm});
            skLineSegment(sketch, "E20.0.17.11", {"start": v(10.38, 1354.14) * mm, "end": v(10.38, 1350.96) * mm});
            skLineSegment(sketch, "E20.0.17.12", {"start": v(19.9, 1354.14) * mm, "end": v(19.9, 1350.96) * mm});
            skLineSegment(sketch, "E20.0.17.13", {"start": v(19.9, 1335.09) * mm, "end": v(19.9, 1331.91) * mm});
            skLineSegment(sketch, "E20.0.17.14", {"start": v(10.38, 1335.09) * mm, "end": v(10.38, 1331.91) * mm});
            skPoint(sketch, "E20.0.18.0", {"position": v(15.14, 1428.75) * mm});
            skArc(sketch, "E20.0.18.1", {"start": v(19.9, 1430.34) * mm, "mid": v(15.14, 1435.1) * mm, "end": v(10.38, 1430.34) * mm});
            skPoint(sketch, "E20.0.18.2", {"position": v(15.14, 1409.7) * mm});
            skPoint(sketch, "E20.0.18.3", {"position": v(15.14, 1390.65) * mm});
            skArc(sketch, "E20.0.18.4", {"start": v(10.38, 1427.16) * mm, "mid": v(15.14, 1422.4) * mm, "end": v(19.9, 1427.16) * mm});
            skCircle(sketch, "E20.0.18.5", {"center": v(15.14, 1390.65) * mm, "radius": 4.76 * mm});
            skCircle(sketch, "E20.0.18.6", {"center": v(15.14, 1371.6) * mm, "radius": 4.76 * mm});
            skArc(sketch, "E20.0.18.7", {"start": v(19.9, 1411.29) * mm, "mid": v(15.14, 1416.05) * mm, "end": v(10.38, 1411.29) * mm});
            skArc(sketch, "E20.0.18.8", {"start": v(10.38, 1408.11) * mm, "mid": v(15.14, 1403.35) * mm, "end": v(19.9, 1408.11) * mm});
            skPoint(sketch, "E20.0.18.9", {"position": v(15.14, 1428.75) * mm});
            skPoint(sketch, "E20.0.18.10", {"position": v(15.14, 1409.7) * mm});
            skLineSegment(sketch, "E20.0.18.11", {"start": v(10.38, 1430.34) * mm, "end": v(10.38, 1427.16) * mm});
            skLineSegment(sketch, "E20.0.18.12", {"start": v(19.9, 1430.34) * mm, "end": v(19.9, 1427.16) * mm});
            skLineSegment(sketch, "E20.0.18.13", {"start": v(19.9, 1411.29) * mm, "end": v(19.9, 1408.11) * mm});
            skLineSegment(sketch, "E20.0.18.14", {"start": v(10.38, 1411.29) * mm, "end": v(10.38, 1408.11) * mm});
            skPoint(sketch, "E20.0.19.0", {"position": v(15.14, 1504.95) * mm});
            skArc(sketch, "E20.0.19.1", {"start": v(19.9, 1506.54) * mm, "mid": v(15.14, 1511.3) * mm, "end": v(10.38, 1506.54) * mm});
            skPoint(sketch, "E20.0.19.2", {"position": v(15.14, 1485.9) * mm});
            skPoint(sketch, "E20.0.19.3", {"position": v(15.14, 1466.85) * mm});
            skArc(sketch, "E20.0.19.4", {"start": v(10.38, 1503.36) * mm, "mid": v(15.14, 1498.6) * mm, "end": v(19.9, 1503.36) * mm});
            skCircle(sketch, "E20.0.19.5", {"center": v(15.14, 1466.85) * mm, "radius": 4.76 * mm});
            skCircle(sketch, "E20.0.19.6", {"center": v(15.14, 1447.8) * mm, "radius": 4.76 * mm});
            skArc(sketch, "E20.0.19.7", {"start": v(19.9, 1487.49) * mm, "mid": v(15.14, 1492.25) * mm, "end": v(10.38, 1487.49) * mm});
            skArc(sketch, "E20.0.19.8", {"start": v(10.38, 1484.31) * mm, "mid": v(15.14, 1479.55) * mm, "end": v(19.9, 1484.31) * mm});
            skPoint(sketch, "E20.0.19.9", {"position": v(15.14, 1504.95) * mm});
            skPoint(sketch, "E20.0.19.10", {"position": v(15.14, 1485.9) * mm});
            skLineSegment(sketch, "E20.0.19.11", {"start": v(10.38, 1506.54) * mm, "end": v(10.38, 1503.36) * mm});
            skLineSegment(sketch, "E20.0.19.12", {"start": v(19.9, 1506.54) * mm, "end": v(19.9, 1503.36) * mm});
            skLineSegment(sketch, "E20.0.19.13", {"start": v(19.9, 1487.49) * mm, "end": v(19.9, 1484.31) * mm});
            skLineSegment(sketch, "E20.0.19.14", {"start": v(10.38, 1487.49) * mm, "end": v(10.38, 1484.31) * mm});
            skPoint(sketch, "E20.0.20.0", {"position": v(15.14, 1581.15) * mm});
            skArc(sketch, "E20.0.20.1", {"start": v(19.9, 1582.74) * mm, "mid": v(15.14, 1587.5) * mm, "end": v(10.38, 1582.74) * mm});
            skPoint(sketch, "E20.0.20.2", {"position": v(15.14, 1562.1) * mm});
            skPoint(sketch, "E20.0.20.3", {"position": v(15.14, 1543.05) * mm});
            skArc(sketch, "E20.0.20.4", {"start": v(10.38, 1579.56) * mm, "mid": v(15.14, 1574.8) * mm, "end": v(19.9, 1579.56) * mm});
            skCircle(sketch, "E20.0.20.5", {"center": v(15.14, 1543.05) * mm, "radius": 4.76 * mm});
            skCircle(sketch, "E20.0.20.6", {"center": v(15.14, 1524) * mm, "radius": 4.76 * mm});
            skArc(sketch, "E20.0.20.7", {"start": v(19.9, 1563.69) * mm, "mid": v(15.14, 1568.45) * mm, "end": v(10.38, 1563.69) * mm});
            skArc(sketch, "E20.0.20.8", {"start": v(10.38, 1560.51) * mm, "mid": v(15.14, 1555.75) * mm, "end": v(19.9, 1560.51) * mm});
            skPoint(sketch, "E20.0.20.9", {"position": v(15.14, 1581.15) * mm});
            skPoint(sketch, "E20.0.20.10", {"position": v(15.14, 1562.1) * mm});
            skLineSegment(sketch, "E20.0.20.11", {"start": v(10.38, 1582.74) * mm, "end": v(10.38, 1579.56) * mm});
            skLineSegment(sketch, "E20.0.20.12", {"start": v(19.9, 1582.74) * mm, "end": v(19.9, 1579.56) * mm});
            skLineSegment(sketch, "E20.0.20.13", {"start": v(19.9, 1563.69) * mm, "end": v(19.9, 1560.51) * mm});
            skLineSegment(sketch, "E20.0.20.14", {"start": v(10.38, 1563.69) * mm, "end": v(10.38, 1560.51) * mm});
            skPoint(sketch, "E20.0.21.0", {"position": v(15.14, 1657.35) * mm});
            skArc(sketch, "E20.0.21.1", {"start": v(19.9, 1658.94) * mm, "mid": v(15.14, 1663.7) * mm, "end": v(10.38, 1658.94) * mm});
            skPoint(sketch, "E20.0.21.2", {"position": v(15.14, 1638.3) * mm});
            skPoint(sketch, "E20.0.21.3", {"position": v(15.14, 1619.25) * mm});
            skArc(sketch, "E20.0.21.4", {"start": v(10.38, 1655.76) * mm, "mid": v(15.14, 1651) * mm, "end": v(19.9, 1655.76) * mm});
            skCircle(sketch, "E20.0.21.5", {"center": v(15.14, 1619.25) * mm, "radius": 4.76 * mm});
            skCircle(sketch, "E20.0.21.6", {"center": v(15.14, 1600.2) * mm, "radius": 4.76 * mm});
            skArc(sketch, "E20.0.21.7", {"start": v(19.9, 1639.89) * mm, "mid": v(15.14, 1644.65) * mm, "end": v(10.38, 1639.89) * mm});
            skArc(sketch, "E20.0.21.8", {"start": v(10.38, 1636.71) * mm, "mid": v(15.14, 1631.95) * mm, "end": v(19.9, 1636.71) * mm});
            skPoint(sketch, "E20.0.21.9", {"position": v(15.14, 1657.35) * mm});
            skPoint(sketch, "E20.0.21.10", {"position": v(15.14, 1638.3) * mm});
            skLineSegment(sketch, "E20.0.21.11", {"start": v(10.38, 1658.94) * mm, "end": v(10.38, 1655.76) * mm});
            skLineSegment(sketch, "E20.0.21.12", {"start": v(19.9, 1658.94) * mm, "end": v(19.9, 1655.76) * mm});
            skLineSegment(sketch, "E20.0.21.13", {"start": v(19.9, 1639.89) * mm, "end": v(19.9, 1636.71) * mm});
            skLineSegment(sketch, "E20.0.21.14", {"start": v(10.38, 1639.89) * mm, "end": v(10.38, 1636.71) * mm});
            skPoint(sketch, "E20.0.22.0", {"position": v(15.14, 1733.55) * mm});
            skArc(sketch, "E20.0.22.1", {"start": v(19.9, 1735.14) * mm, "mid": v(15.14, 1739.9) * mm, "end": v(10.38, 1735.14) * mm});
            skPoint(sketch, "E20.0.22.2", {"position": v(15.14, 1714.5) * mm});
            skPoint(sketch, "E20.0.22.3", {"position": v(15.14, 1695.45) * mm});
            skArc(sketch, "E20.0.22.4", {"start": v(10.38, 1731.96) * mm, "mid": v(15.14, 1727.2) * mm, "end": v(19.9, 1731.96) * mm});
            skCircle(sketch, "E20.0.22.5", {"center": v(15.14, 1695.45) * mm, "radius": 4.76 * mm});
            skCircle(sketch, "E20.0.22.6", {"center": v(15.14, 1676.4) * mm, "radius": 4.76 * mm});
            skArc(sketch, "E20.0.22.7", {"start": v(19.9, 1716.09) * mm, "mid": v(15.14, 1720.85) * mm, "end": v(10.38, 1716.09) * mm});
            skArc(sketch, "E20.0.22.8", {"start": v(10.38, 1712.91) * mm, "mid": v(15.14, 1708.15) * mm, "end": v(19.9, 1712.91) * mm});
            skPoint(sketch, "E20.0.22.9", {"position": v(15.14, 1733.55) * mm});
            skPoint(sketch, "E20.0.22.10", {"position": v(15.14, 1714.5) * mm});
            skLineSegment(sketch, "E20.0.22.11", {"start": v(10.38, 1735.14) * mm, "end": v(10.38, 1731.96) * mm});
            skLineSegment(sketch, "E20.0.22.12", {"start": v(19.9, 1735.14) * mm, "end": v(19.9, 1731.96) * mm});
            skLineSegment(sketch, "E20.0.22.13", {"start": v(19.9, 1716.09) * mm, "end": v(19.9, 1712.91) * mm});
            skLineSegment(sketch, "E20.0.22.14", {"start": v(10.38, 1716.09) * mm, "end": v(10.38, 1712.91) * mm});
            skPoint(sketch, "E20.0.23.0", {"position": v(15.14, 1809.75) * mm});
            skArc(sketch, "E20.0.23.1", {"start": v(19.9, 1811.34) * mm, "mid": v(15.14, 1816.1) * mm, "end": v(10.38, 1811.34) * mm});
            skPoint(sketch, "E20.0.23.2", {"position": v(15.14, 1790.7) * mm});
            skPoint(sketch, "E20.0.23.3", {"position": v(15.14, 1771.65) * mm});
            skArc(sketch, "E20.0.23.4", {"start": v(10.38, 1808.16) * mm, "mid": v(15.14, 1803.4) * mm, "end": v(19.9, 1808.16) * mm});
            skCircle(sketch, "E20.0.23.5", {"center": v(15.14, 1771.65) * mm, "radius": 4.76 * mm});
            skCircle(sketch, "E20.0.23.6", {"center": v(15.14, 1752.6) * mm, "radius": 4.76 * mm});
            skArc(sketch, "E20.0.23.7", {"start": v(19.9, 1792.29) * mm, "mid": v(15.14, 1797.05) * mm, "end": v(10.38, 1792.29) * mm});
            skArc(sketch, "E20.0.23.8", {"start": v(10.38, 1789.11) * mm, "mid": v(15.14, 1784.35) * mm, "end": v(19.9, 1789.11) * mm});
            skPoint(sketch, "E20.0.23.9", {"position": v(15.14, 1809.75) * mm});
            skPoint(sketch, "E20.0.23.10", {"position": v(15.14, 1790.7) * mm});
            skLineSegment(sketch, "E20.0.23.11", {"start": v(10.38, 1811.34) * mm, "end": v(10.38, 1808.16) * mm});
            skLineSegment(sketch, "E20.0.23.12", {"start": v(19.9, 1811.34) * mm, "end": v(19.9, 1808.16) * mm});
            skLineSegment(sketch, "E20.0.23.13", {"start": v(19.9, 1792.29) * mm, "end": v(19.9, 1789.11) * mm});
            skLineSegment(sketch, "E20.0.23.14", {"start": v(10.38, 1792.29) * mm, "end": v(10.38, 1789.11) * mm});
            skLineSegment(sketch, "E20.direction1", {"start": v(15.14, 0) * mm, "end": v(40.54, 0) * mm, "construction": true});
            skLineSegment(sketch, "E20.direction2", {"start": v(15.14, 0) * mm, "end": v(15.14, 76.2) * mm, "construction": true});
            skSolve(sketch);
        }
        {
            var Q0;
            Q0=makeQuery(id+"F2.opExtrude","SWEPT_FACE",FACE,{"disambiguationData":[OSD([sQuery(id+"F1.wireOp",EDGE,"E4")])]});
            var sketch = newSketch(context, id + "F4", { "sketchPlane" : qUnion([Q0])});
            skPoint(sketch, "E21", {"position": v(-15.14, 19.05) * mm});
            skLineSegment(sketch, "E22", {"start": v(-15.14, 0) * mm, "end": v(-15.14, 203.2) * mm, "construction": true});
            skCircle(sketch, "E23", {"center": v(-15.14, 19.05) * mm, "radius": 4.76 * mm});
            skCircle(sketch, "E24", {"center": v(-15.14, 0) * mm, "radius": 4.76 * mm});
            skPoint(sketch, "E25", {"position": v(-15.14, 38.1) * mm});
            skPoint(sketch, "E26", {"position": v(-15.14, 57.15) * mm});
            skArc(sketch, "E27", {"start": v(-10.38, 39.69) * mm, "mid": v(-15.14, 44.45) * mm, "end": v(-19.9, 39.69) * mm});
            skArc(sketch, "E28", {"start": v(-19.9, 36.51) * mm, "mid": v(-15.14, 31.75) * mm, "end": v(-10.38, 36.51) * mm});
            skLineSegment(sketch, "E29", {"start": v(-10.38, 39.69) * mm, "end": v(-10.38, 36.51) * mm});
            skLineSegment(sketch, "E30", {"start": v(-19.9, 39.69) * mm, "end": v(-19.9, 36.51) * mm});
            skArc(sketch, "E31", {"start": v(-10.38, 58.74) * mm, "mid": v(-15.14, 63.5) * mm, "end": v(-19.9, 58.74) * mm});
            skArc(sketch, "E32", {"start": v(-19.9, 55.56) * mm, "mid": v(-15.14, 50.8) * mm, "end": v(-10.38, 55.56) * mm});
            skLineSegment(sketch, "E33", {"start": v(-10.38, 58.74) * mm, "end": v(-10.38, 55.56) * mm});
            skLineSegment(sketch, "E34", {"start": v(-19.9, 58.74) * mm, "end": v(-19.9, 55.56) * mm});
            skPoint(sketch, "E35.0.1.0", {"position": v(-15.14, 133.35) * mm});
            skArc(sketch, "E35.0.1.1", {"start": v(-10.38, 134.94) * mm, "mid": v(-15.14, 139.7) * mm, "end": v(-19.9, 134.94) * mm});
            skPoint(sketch, "E35.0.1.2", {"position": v(-15.14, 114.3) * mm});
            skPoint(sketch, "E35.0.1.3", {"position": v(-15.14, 95.25) * mm});
            skArc(sketch, "E35.0.1.4", {"start": v(-19.9, 131.76) * mm, "mid": v(-15.14, 127) * mm, "end": v(-10.38, 131.76) * mm});
            skCircle(sketch, "E35.0.1.5", {"center": v(-15.14, 95.25) * mm, "radius": 4.76 * mm});
            skCircle(sketch, "E35.0.1.6", {"center": v(-15.14, 76.2) * mm, "radius": 4.76 * mm});
            skArc(sketch, "E35.0.1.7", {"start": v(-10.38, 115.89) * mm, "mid": v(-15.14, 120.65) * mm, "end": v(-19.9, 115.89) * mm});
            skArc(sketch, "E35.0.1.8", {"start": v(-19.9, 112.71) * mm, "mid": v(-15.14, 107.95) * mm, "end": v(-10.38, 112.71) * mm});
            skPoint(sketch, "E35.0.1.9", {"position": v(-15.14, 133.35) * mm});
            skPoint(sketch, "E35.0.1.10", {"position": v(-15.14, 114.3) * mm});
            skLineSegment(sketch, "E35.0.1.11", {"start": v(-19.9, 134.94) * mm, "end": v(-19.9, 131.76) * mm});
            skLineSegment(sketch, "E35.0.1.12", {"start": v(-10.38, 134.94) * mm, "end": v(-10.38, 131.76) * mm});
            skLineSegment(sketch, "E35.0.1.13", {"start": v(-10.38, 115.89) * mm, "end": v(-10.38, 112.71) * mm});
            skLineSegment(sketch, "E35.0.1.14", {"start": v(-19.9, 115.89) * mm, "end": v(-19.9, 112.71) * mm});
            skPoint(sketch, "E35.0.2.0", {"position": v(-15.14, 209.55) * mm});
            skArc(sketch, "E35.0.2.1", {"start": v(-10.38, 211.14) * mm, "mid": v(-15.14, 215.9) * mm, "end": v(-19.9, 211.14) * mm});
            skPoint(sketch, "E35.0.2.2", {"position": v(-15.14, 190.5) * mm});
            skPoint(sketch, "E35.0.2.3", {"position": v(-15.14, 171.45) * mm});
            skArc(sketch, "E35.0.2.4", {"start": v(-19.9, 207.96) * mm, "mid": v(-15.14, 203.2) * mm, "end": v(-10.38, 207.96) * mm});
            skCircle(sketch, "E35.0.2.5", {"center": v(-15.14, 171.45) * mm, "radius": 4.76 * mm});
            skCircle(sketch, "E35.0.2.6", {"center": v(-15.14, 152.4) * mm, "radius": 4.76 * mm});
            skArc(sketch, "E35.0.2.7", {"start": v(-10.38, 192.09) * mm, "mid": v(-15.14, 196.85) * mm, "end": v(-19.9, 192.09) * mm});
            skArc(sketch, "E35.0.2.8", {"start": v(-19.9, 188.91) * mm, "mid": v(-15.14, 184.15) * mm, "end": v(-10.38, 188.91) * mm});
            skPoint(sketch, "E35.0.2.9", {"position": v(-15.14, 209.55) * mm});
            skPoint(sketch, "E35.0.2.10", {"position": v(-15.14, 190.5) * mm});
            skLineSegment(sketch, "E35.0.2.11", {"start": v(-19.9, 211.14) * mm, "end": v(-19.9, 207.96) * mm});
            skLineSegment(sketch, "E35.0.2.12", {"start": v(-10.38, 211.14) * mm, "end": v(-10.38, 207.96) * mm});
            skLineSegment(sketch, "E35.0.2.13", {"start": v(-10.38, 192.09) * mm, "end": v(-10.38, 188.91) * mm});
            skLineSegment(sketch, "E35.0.2.14", {"start": v(-19.9, 192.09) * mm, "end": v(-19.9, 188.91) * mm});
            skPoint(sketch, "E35.0.3.0", {"position": v(-15.14, 285.75) * mm});
            skArc(sketch, "E35.0.3.1", {"start": v(-10.38, 287.34) * mm, "mid": v(-15.14, 292.1) * mm, "end": v(-19.9, 287.34) * mm});
            skPoint(sketch, "E35.0.3.2", {"position": v(-15.14, 266.7) * mm});
            skPoint(sketch, "E35.0.3.3", {"position": v(-15.14, 247.65) * mm});
            skArc(sketch, "E35.0.3.4", {"start": v(-19.9, 284.16) * mm, "mid": v(-15.14, 279.4) * mm, "end": v(-10.38, 284.16) * mm});
            skCircle(sketch, "E35.0.3.5", {"center": v(-15.14, 247.65) * mm, "radius": 4.76 * mm});
            skCircle(sketch, "E35.0.3.6", {"center": v(-15.14, 228.6) * mm, "radius": 4.76 * mm});
            skArc(sketch, "E35.0.3.7", {"start": v(-10.38, 268.29) * mm, "mid": v(-15.14, 273.05) * mm, "end": v(-19.9, 268.29) * mm});
            skArc(sketch, "E35.0.3.8", {"start": v(-19.9, 265.11) * mm, "mid": v(-15.14, 260.35) * mm, "end": v(-10.38, 265.11) * mm});
            skPoint(sketch, "E35.0.3.9", {"position": v(-15.14, 285.75) * mm});
            skPoint(sketch, "E35.0.3.10", {"position": v(-15.14, 266.7) * mm});
            skLineSegment(sketch, "E35.0.3.11", {"start": v(-19.9, 287.34) * mm, "end": v(-19.9, 284.16) * mm});
            skLineSegment(sketch, "E35.0.3.12", {"start": v(-10.38, 287.34) * mm, "end": v(-10.38, 284.16) * mm});
            skLineSegment(sketch, "E35.0.3.13", {"start": v(-10.38, 268.29) * mm, "end": v(-10.38, 265.11) * mm});
            skLineSegment(sketch, "E35.0.3.14", {"start": v(-19.9, 268.29) * mm, "end": v(-19.9, 265.11) * mm});
            skPoint(sketch, "E35.0.4.0", {"position": v(-15.14, 361.95) * mm});
            skArc(sketch, "E35.0.4.1", {"start": v(-10.38, 363.54) * mm, "mid": v(-15.14, 368.3) * mm, "end": v(-19.9, 363.54) * mm});
            skPoint(sketch, "E35.0.4.2", {"position": v(-15.14, 342.9) * mm});
            skPoint(sketch, "E35.0.4.3", {"position": v(-15.14, 323.85) * mm});
            skArc(sketch, "E35.0.4.4", {"start": v(-19.9, 360.36) * mm, "mid": v(-15.14, 355.6) * mm, "end": v(-10.38, 360.36) * mm});
            skCircle(sketch, "E35.0.4.5", {"center": v(-15.14, 323.85) * mm, "radius": 4.76 * mm});
            skCircle(sketch, "E35.0.4.6", {"center": v(-15.14, 304.8) * mm, "radius": 4.76 * mm});
            skArc(sketch, "E35.0.4.7", {"start": v(-10.38, 344.49) * mm, "mid": v(-15.14, 349.25) * mm, "end": v(-19.9, 344.49) * mm});
            skArc(sketch, "E35.0.4.8", {"start": v(-19.9, 341.31) * mm, "mid": v(-15.14, 336.55) * mm, "end": v(-10.38, 341.31) * mm});
            skPoint(sketch, "E35.0.4.9", {"position": v(-15.14, 361.95) * mm});
            skPoint(sketch, "E35.0.4.10", {"position": v(-15.14, 342.9) * mm});
            skLineSegment(sketch, "E35.0.4.11", {"start": v(-19.9, 363.54) * mm, "end": v(-19.9, 360.36) * mm});
            skLineSegment(sketch, "E35.0.4.12", {"start": v(-10.38, 363.54) * mm, "end": v(-10.38, 360.36) * mm});
            skLineSegment(sketch, "E35.0.4.13", {"start": v(-10.38, 344.49) * mm, "end": v(-10.38, 341.31) * mm});
            skLineSegment(sketch, "E35.0.4.14", {"start": v(-19.9, 344.49) * mm, "end": v(-19.9, 341.31) * mm});
            skPoint(sketch, "E35.0.5.0", {"position": v(-15.14, 438.15) * mm});
            skArc(sketch, "E35.0.5.1", {"start": v(-10.38, 439.74) * mm, "mid": v(-15.14, 444.5) * mm, "end": v(-19.9, 439.74) * mm});
            skPoint(sketch, "E35.0.5.2", {"position": v(-15.14, 419.1) * mm});
            skPoint(sketch, "E35.0.5.3", {"position": v(-15.14, 400.05) * mm});
            skArc(sketch, "E35.0.5.4", {"start": v(-19.9, 436.56) * mm, "mid": v(-15.14, 431.8) * mm, "end": v(-10.38, 436.56) * mm});
            skCircle(sketch, "E35.0.5.5", {"center": v(-15.14, 400.05) * mm, "radius": 4.76 * mm});
            skCircle(sketch, "E35.0.5.6", {"center": v(-15.14, 381) * mm, "radius": 4.76 * mm});
            skArc(sketch, "E35.0.5.7", {"start": v(-10.38, 420.69) * mm, "mid": v(-15.14, 425.45) * mm, "end": v(-19.9, 420.69) * mm});
            skArc(sketch, "E35.0.5.8", {"start": v(-19.9, 417.51) * mm, "mid": v(-15.14, 412.75) * mm, "end": v(-10.38, 417.51) * mm});
            skPoint(sketch, "E35.0.5.9", {"position": v(-15.14, 438.15) * mm});
            skPoint(sketch, "E35.0.5.10", {"position": v(-15.14, 419.1) * mm});
            skLineSegment(sketch, "E35.0.5.11", {"start": v(-19.9, 439.74) * mm, "end": v(-19.9, 436.56) * mm});
            skLineSegment(sketch, "E35.0.5.12", {"start": v(-10.38, 439.74) * mm, "end": v(-10.38, 436.56) * mm});
            skLineSegment(sketch, "E35.0.5.13", {"start": v(-10.38, 420.69) * mm, "end": v(-10.38, 417.51) * mm});
            skLineSegment(sketch, "E35.0.5.14", {"start": v(-19.9, 420.69) * mm, "end": v(-19.9, 417.51) * mm});
            skPoint(sketch, "E35.0.6.0", {"position": v(-15.14, 514.35) * mm});
            skArc(sketch, "E35.0.6.1", {"start": v(-10.38, 515.94) * mm, "mid": v(-15.14, 520.7) * mm, "end": v(-19.9, 515.94) * mm});
            skPoint(sketch, "E35.0.6.2", {"position": v(-15.14, 495.3) * mm});
            skPoint(sketch, "E35.0.6.3", {"position": v(-15.14, 476.25) * mm});
            skArc(sketch, "E35.0.6.4", {"start": v(-19.9, 512.76) * mm, "mid": v(-15.14, 508) * mm, "end": v(-10.38, 512.76) * mm});
            skCircle(sketch, "E35.0.6.5", {"center": v(-15.14, 476.25) * mm, "radius": 4.76 * mm});
            skCircle(sketch, "E35.0.6.6", {"center": v(-15.14, 457.2) * mm, "radius": 4.76 * mm});
            skArc(sketch, "E35.0.6.7", {"start": v(-10.38, 496.89) * mm, "mid": v(-15.14, 501.65) * mm, "end": v(-19.9, 496.89) * mm});
            skArc(sketch, "E35.0.6.8", {"start": v(-19.9, 493.71) * mm, "mid": v(-15.14, 488.95) * mm, "end": v(-10.38, 493.71) * mm});
            skPoint(sketch, "E35.0.6.9", {"position": v(-15.14, 514.35) * mm});
            skPoint(sketch, "E35.0.6.10", {"position": v(-15.14, 495.3) * mm});
            skLineSegment(sketch, "E35.0.6.11", {"start": v(-19.9, 515.94) * mm, "end": v(-19.9, 512.76) * mm});
            skLineSegment(sketch, "E35.0.6.12", {"start": v(-10.38, 515.94) * mm, "end": v(-10.38, 512.76) * mm});
            skLineSegment(sketch, "E35.0.6.13", {"start": v(-10.38, 496.89) * mm, "end": v(-10.38, 493.71) * mm});
            skLineSegment(sketch, "E35.0.6.14", {"start": v(-19.9, 496.89) * mm, "end": v(-19.9, 493.71) * mm});
            skPoint(sketch, "E35.0.7.0", {"position": v(-15.14, 590.55) * mm});
            skArc(sketch, "E35.0.7.1", {"start": v(-10.38, 592.14) * mm, "mid": v(-15.14, 596.9) * mm, "end": v(-19.9, 592.14) * mm});
            skPoint(sketch, "E35.0.7.2", {"position": v(-15.14, 571.5) * mm});
            skPoint(sketch, "E35.0.7.3", {"position": v(-15.14, 552.45) * mm});
            skArc(sketch, "E35.0.7.4", {"start": v(-19.9, 588.96) * mm, "mid": v(-15.14, 584.2) * mm, "end": v(-10.38, 588.96) * mm});
            skCircle(sketch, "E35.0.7.5", {"center": v(-15.14, 552.45) * mm, "radius": 4.76 * mm});
            skCircle(sketch, "E35.0.7.6", {"center": v(-15.14, 533.4) * mm, "radius": 4.76 * mm});
            skArc(sketch, "E35.0.7.7", {"start": v(-10.38, 573.09) * mm, "mid": v(-15.14, 577.85) * mm, "end": v(-19.9, 573.09) * mm});
            skArc(sketch, "E35.0.7.8", {"start": v(-19.9, 569.91) * mm, "mid": v(-15.14, 565.15) * mm, "end": v(-10.38, 569.91) * mm});
            skPoint(sketch, "E35.0.7.9", {"position": v(-15.14, 590.55) * mm});
            skPoint(sketch, "E35.0.7.10", {"position": v(-15.14, 571.5) * mm});
            skLineSegment(sketch, "E35.0.7.11", {"start": v(-19.9, 592.14) * mm, "end": v(-19.9, 588.96) * mm});
            skLineSegment(sketch, "E35.0.7.12", {"start": v(-10.38, 592.14) * mm, "end": v(-10.38, 588.96) * mm});
            skLineSegment(sketch, "E35.0.7.13", {"start": v(-10.38, 573.09) * mm, "end": v(-10.38, 569.91) * mm});
            skLineSegment(sketch, "E35.0.7.14", {"start": v(-19.9, 573.09) * mm, "end": v(-19.9, 569.91) * mm});
            skPoint(sketch, "E35.0.8.0", {"position": v(-15.14, 666.75) * mm});
            skArc(sketch, "E35.0.8.1", {"start": v(-10.38, 668.34) * mm, "mid": v(-15.14, 673.1) * mm, "end": v(-19.9, 668.34) * mm});
            skPoint(sketch, "E35.0.8.2", {"position": v(-15.14, 647.7) * mm});
            skPoint(sketch, "E35.0.8.3", {"position": v(-15.14, 628.65) * mm});
            skArc(sketch, "E35.0.8.4", {"start": v(-19.9, 665.16) * mm, "mid": v(-15.14, 660.4) * mm, "end": v(-10.38, 665.16) * mm});
            skCircle(sketch, "E35.0.8.5", {"center": v(-15.14, 628.65) * mm, "radius": 4.76 * mm});
            skCircle(sketch, "E35.0.8.6", {"center": v(-15.14, 609.6) * mm, "radius": 4.76 * mm});
            skArc(sketch, "E35.0.8.7", {"start": v(-10.38, 649.29) * mm, "mid": v(-15.14, 654.05) * mm, "end": v(-19.9, 649.29) * mm});
            skArc(sketch, "E35.0.8.8", {"start": v(-19.9, 646.11) * mm, "mid": v(-15.14, 641.35) * mm, "end": v(-10.38, 646.11) * mm});
            skPoint(sketch, "E35.0.8.9", {"position": v(-15.14, 666.75) * mm});
            skPoint(sketch, "E35.0.8.10", {"position": v(-15.14, 647.7) * mm});
            skLineSegment(sketch, "E35.0.8.11", {"start": v(-19.9, 668.34) * mm, "end": v(-19.9, 665.16) * mm});
            skLineSegment(sketch, "E35.0.8.12", {"start": v(-10.38, 668.34) * mm, "end": v(-10.38, 665.16) * mm});
            skLineSegment(sketch, "E35.0.8.13", {"start": v(-10.38, 649.29) * mm, "end": v(-10.38, 646.11) * mm});
            skLineSegment(sketch, "E35.0.8.14", {"start": v(-19.9, 649.29) * mm, "end": v(-19.9, 646.11) * mm});
            skPoint(sketch, "E35.0.9.0", {"position": v(-15.14, 742.95) * mm});
            skArc(sketch, "E35.0.9.1", {"start": v(-10.38, 744.54) * mm, "mid": v(-15.14, 749.3) * mm, "end": v(-19.9, 744.54) * mm});
            skPoint(sketch, "E35.0.9.2", {"position": v(-15.14, 723.9) * mm});
            skPoint(sketch, "E35.0.9.3", {"position": v(-15.14, 704.85) * mm});
            skArc(sketch, "E35.0.9.4", {"start": v(-19.9, 741.36) * mm, "mid": v(-15.14, 736.6) * mm, "end": v(-10.38, 741.36) * mm});
            skCircle(sketch, "E35.0.9.5", {"center": v(-15.14, 704.85) * mm, "radius": 4.76 * mm});
            skCircle(sketch, "E35.0.9.6", {"center": v(-15.14, 685.8) * mm, "radius": 4.76 * mm});
            skArc(sketch, "E35.0.9.7", {"start": v(-10.38, 725.49) * mm, "mid": v(-15.14, 730.25) * mm, "end": v(-19.9, 725.49) * mm});
            skArc(sketch, "E35.0.9.8", {"start": v(-19.9, 722.31) * mm, "mid": v(-15.14, 717.55) * mm, "end": v(-10.38, 722.31) * mm});
            skPoint(sketch, "E35.0.9.9", {"position": v(-15.14, 742.95) * mm});
            skPoint(sketch, "E35.0.9.10", {"position": v(-15.14, 723.9) * mm});
            skLineSegment(sketch, "E35.0.9.11", {"start": v(-19.9, 744.54) * mm, "end": v(-19.9, 741.36) * mm});
            skLineSegment(sketch, "E35.0.9.12", {"start": v(-10.38, 744.54) * mm, "end": v(-10.38, 741.36) * mm});
            skLineSegment(sketch, "E35.0.9.13", {"start": v(-10.38, 725.49) * mm, "end": v(-10.38, 722.31) * mm});
            skLineSegment(sketch, "E35.0.9.14", {"start": v(-19.9, 725.49) * mm, "end": v(-19.9, 722.31) * mm});
            skPoint(sketch, "E35.0.10.0", {"position": v(-15.14, 819.15) * mm});
            skArc(sketch, "E35.0.10.1", {"start": v(-10.38, 820.74) * mm, "mid": v(-15.14, 825.5) * mm, "end": v(-19.9, 820.74) * mm});
            skPoint(sketch, "E35.0.10.2", {"position": v(-15.14, 800.1) * mm});
            skPoint(sketch, "E35.0.10.3", {"position": v(-15.14, 781.05) * mm});
            skArc(sketch, "E35.0.10.4", {"start": v(-19.9, 817.56) * mm, "mid": v(-15.14, 812.8) * mm, "end": v(-10.38, 817.56) * mm});
            skCircle(sketch, "E35.0.10.5", {"center": v(-15.14, 781.05) * mm, "radius": 4.76 * mm});
            skCircle(sketch, "E35.0.10.6", {"center": v(-15.14, 762) * mm, "radius": 4.76 * mm});
            skArc(sketch, "E35.0.10.7", {"start": v(-10.38, 801.69) * mm, "mid": v(-15.14, 806.45) * mm, "end": v(-19.9, 801.69) * mm});
            skArc(sketch, "E35.0.10.8", {"start": v(-19.9, 798.51) * mm, "mid": v(-15.14, 793.75) * mm, "end": v(-10.38, 798.51) * mm});
            skPoint(sketch, "E35.0.10.9", {"position": v(-15.14, 819.15) * mm});
            skPoint(sketch, "E35.0.10.10", {"position": v(-15.14, 800.1) * mm});
            skLineSegment(sketch, "E35.0.10.11", {"start": v(-19.9, 820.74) * mm, "end": v(-19.9, 817.56) * mm});
            skLineSegment(sketch, "E35.0.10.12", {"start": v(-10.38, 820.74) * mm, "end": v(-10.38, 817.56) * mm});
            skLineSegment(sketch, "E35.0.10.13", {"start": v(-10.38, 801.69) * mm, "end": v(-10.38, 798.51) * mm});
            skLineSegment(sketch, "E35.0.10.14", {"start": v(-19.9, 801.69) * mm, "end": v(-19.9, 798.51) * mm});
            skPoint(sketch, "E35.0.11.0", {"position": v(-15.14, 895.35) * mm});
            skArc(sketch, "E35.0.11.1", {"start": v(-10.38, 896.94) * mm, "mid": v(-15.14, 901.7) * mm, "end": v(-19.9, 896.94) * mm});
            skPoint(sketch, "E35.0.11.2", {"position": v(-15.14, 876.3) * mm});
            skPoint(sketch, "E35.0.11.3", {"position": v(-15.14, 857.25) * mm});
            skArc(sketch, "E35.0.11.4", {"start": v(-19.9, 893.76) * mm, "mid": v(-15.14, 889) * mm, "end": v(-10.38, 893.76) * mm});
            skCircle(sketch, "E35.0.11.5", {"center": v(-15.14, 857.25) * mm, "radius": 4.76 * mm});
            skCircle(sketch, "E35.0.11.6", {"center": v(-15.14, 838.2) * mm, "radius": 4.76 * mm});
            skArc(sketch, "E35.0.11.7", {"start": v(-10.38, 877.89) * mm, "mid": v(-15.14, 882.65) * mm, "end": v(-19.9, 877.89) * mm});
            skArc(sketch, "E35.0.11.8", {"start": v(-19.9, 874.71) * mm, "mid": v(-15.14, 869.95) * mm, "end": v(-10.38, 874.71) * mm});
            skPoint(sketch, "E35.0.11.9", {"position": v(-15.14, 895.35) * mm});
            skPoint(sketch, "E35.0.11.10", {"position": v(-15.14, 876.3) * mm});
            skLineSegment(sketch, "E35.0.11.11", {"start": v(-19.9, 896.94) * mm, "end": v(-19.9, 893.76) * mm});
            skLineSegment(sketch, "E35.0.11.12", {"start": v(-10.38, 896.94) * mm, "end": v(-10.38, 893.76) * mm});
            skLineSegment(sketch, "E35.0.11.13", {"start": v(-10.38, 877.89) * mm, "end": v(-10.38, 874.71) * mm});
            skLineSegment(sketch, "E35.0.11.14", {"start": v(-19.9, 877.89) * mm, "end": v(-19.9, 874.71) * mm});
            skPoint(sketch, "E35.0.12.0", {"position": v(-15.14, 971.55) * mm});
            skArc(sketch, "E35.0.12.1", {"start": v(-10.38, 973.14) * mm, "mid": v(-15.14, 977.9) * mm, "end": v(-19.9, 973.14) * mm});
            skPoint(sketch, "E35.0.12.2", {"position": v(-15.14, 952.5) * mm});
            skPoint(sketch, "E35.0.12.3", {"position": v(-15.14, 933.45) * mm});
            skArc(sketch, "E35.0.12.4", {"start": v(-19.9, 969.96) * mm, "mid": v(-15.14, 965.2) * mm, "end": v(-10.38, 969.96) * mm});
            skCircle(sketch, "E35.0.12.5", {"center": v(-15.14, 933.45) * mm, "radius": 4.76 * mm});
            skCircle(sketch, "E35.0.12.6", {"center": v(-15.14, 914.4) * mm, "radius": 4.76 * mm});
            skArc(sketch, "E35.0.12.7", {"start": v(-10.38, 954.09) * mm, "mid": v(-15.14, 958.85) * mm, "end": v(-19.9, 954.09) * mm});
            skArc(sketch, "E35.0.12.8", {"start": v(-19.9, 950.91) * mm, "mid": v(-15.14, 946.15) * mm, "end": v(-10.38, 950.91) * mm});
            skPoint(sketch, "E35.0.12.9", {"position": v(-15.14, 971.55) * mm});
            skPoint(sketch, "E35.0.12.10", {"position": v(-15.14, 952.5) * mm});
            skLineSegment(sketch, "E35.0.12.11", {"start": v(-19.9, 973.14) * mm, "end": v(-19.9, 969.96) * mm});
            skLineSegment(sketch, "E35.0.12.12", {"start": v(-10.38, 973.14) * mm, "end": v(-10.38, 969.96) * mm});
            skLineSegment(sketch, "E35.0.12.13", {"start": v(-10.38, 954.09) * mm, "end": v(-10.38, 950.91) * mm});
            skLineSegment(sketch, "E35.0.12.14", {"start": v(-19.9, 954.09) * mm, "end": v(-19.9, 950.91) * mm});
            skPoint(sketch, "E35.0.13.0", {"position": v(-15.14, 1047.75) * mm});
            skArc(sketch, "E35.0.13.1", {"start": v(-10.38, 1049.34) * mm, "mid": v(-15.14, 1054.1) * mm, "end": v(-19.9, 1049.34) * mm});
            skPoint(sketch, "E35.0.13.2", {"position": v(-15.14, 1028.7) * mm});
            skPoint(sketch, "E35.0.13.3", {"position": v(-15.14, 1009.65) * mm});
            skArc(sketch, "E35.0.13.4", {"start": v(-19.9, 1046.16) * mm, "mid": v(-15.14, 1041.4) * mm, "end": v(-10.38, 1046.16) * mm});
            skCircle(sketch, "E35.0.13.5", {"center": v(-15.14, 1009.65) * mm, "radius": 4.76 * mm});
            skCircle(sketch, "E35.0.13.6", {"center": v(-15.14, 990.6) * mm, "radius": 4.76 * mm});
            skArc(sketch, "E35.0.13.7", {"start": v(-10.38, 1030.29) * mm, "mid": v(-15.14, 1035.05) * mm, "end": v(-19.9, 1030.29) * mm});
            skArc(sketch, "E35.0.13.8", {"start": v(-19.9, 1027.11) * mm, "mid": v(-15.14, 1022.35) * mm, "end": v(-10.38, 1027.11) * mm});
            skPoint(sketch, "E35.0.13.9", {"position": v(-15.14, 1047.75) * mm});
            skPoint(sketch, "E35.0.13.10", {"position": v(-15.14, 1028.7) * mm});
            skLineSegment(sketch, "E35.0.13.11", {"start": v(-19.9, 1049.34) * mm, "end": v(-19.9, 1046.16) * mm});
            skLineSegment(sketch, "E35.0.13.12", {"start": v(-10.38, 1049.34) * mm, "end": v(-10.38, 1046.16) * mm});
            skLineSegment(sketch, "E35.0.13.13", {"start": v(-10.38, 1030.29) * mm, "end": v(-10.38, 1027.11) * mm});
            skLineSegment(sketch, "E35.0.13.14", {"start": v(-19.9, 1030.29) * mm, "end": v(-19.9, 1027.11) * mm});
            skPoint(sketch, "E35.0.14.0", {"position": v(-15.14, 1123.95) * mm});
            skArc(sketch, "E35.0.14.1", {"start": v(-10.38, 1125.54) * mm, "mid": v(-15.14, 1130.3) * mm, "end": v(-19.9, 1125.54) * mm});
            skPoint(sketch, "E35.0.14.2", {"position": v(-15.14, 1104.9) * mm});
            skPoint(sketch, "E35.0.14.3", {"position": v(-15.14, 1085.85) * mm});
            skArc(sketch, "E35.0.14.4", {"start": v(-19.9, 1122.36) * mm, "mid": v(-15.14, 1117.6) * mm, "end": v(-10.38, 1122.36) * mm});
            skCircle(sketch, "E35.0.14.5", {"center": v(-15.14, 1085.85) * mm, "radius": 4.76 * mm});
            skCircle(sketch, "E35.0.14.6", {"center": v(-15.14, 1066.8) * mm, "radius": 4.76 * mm});
            skArc(sketch, "E35.0.14.7", {"start": v(-10.38, 1106.49) * mm, "mid": v(-15.14, 1111.25) * mm, "end": v(-19.9, 1106.49) * mm});
            skArc(sketch, "E35.0.14.8", {"start": v(-19.9, 1103.31) * mm, "mid": v(-15.14, 1098.55) * mm, "end": v(-10.38, 1103.31) * mm});
            skPoint(sketch, "E35.0.14.9", {"position": v(-15.14, 1123.95) * mm});
            skPoint(sketch, "E35.0.14.10", {"position": v(-15.14, 1104.9) * mm});
            skLineSegment(sketch, "E35.0.14.11", {"start": v(-19.9, 1125.54) * mm, "end": v(-19.9, 1122.36) * mm});
            skLineSegment(sketch, "E35.0.14.12", {"start": v(-10.38, 1125.54) * mm, "end": v(-10.38, 1122.36) * mm});
            skLineSegment(sketch, "E35.0.14.13", {"start": v(-10.38, 1106.49) * mm, "end": v(-10.38, 1103.31) * mm});
            skLineSegment(sketch, "E35.0.14.14", {"start": v(-19.9, 1106.49) * mm, "end": v(-19.9, 1103.31) * mm});
            skPoint(sketch, "E35.0.15.0", {"position": v(-15.14, 1200.15) * mm});
            skArc(sketch, "E35.0.15.1", {"start": v(-10.38, 1201.74) * mm, "mid": v(-15.14, 1206.5) * mm, "end": v(-19.9, 1201.74) * mm});
            skPoint(sketch, "E35.0.15.2", {"position": v(-15.14, 1181.1) * mm});
            skPoint(sketch, "E35.0.15.3", {"position": v(-15.14, 1162.05) * mm});
            skArc(sketch, "E35.0.15.4", {"start": v(-19.9, 1198.56) * mm, "mid": v(-15.14, 1193.8) * mm, "end": v(-10.38, 1198.56) * mm});
            skCircle(sketch, "E35.0.15.5", {"center": v(-15.14, 1162.05) * mm, "radius": 4.76 * mm});
            skCircle(sketch, "E35.0.15.6", {"center": v(-15.14, 1143) * mm, "radius": 4.76 * mm});
            skArc(sketch, "E35.0.15.7", {"start": v(-10.38, 1182.69) * mm, "mid": v(-15.14, 1187.45) * mm, "end": v(-19.9, 1182.69) * mm});
            skArc(sketch, "E35.0.15.8", {"start": v(-19.9, 1179.51) * mm, "mid": v(-15.14, 1174.75) * mm, "end": v(-10.38, 1179.51) * mm});
            skPoint(sketch, "E35.0.15.9", {"position": v(-15.14, 1200.15) * mm});
            skPoint(sketch, "E35.0.15.10", {"position": v(-15.14, 1181.1) * mm});
            skLineSegment(sketch, "E35.0.15.11", {"start": v(-19.9, 1201.74) * mm, "end": v(-19.9, 1198.56) * mm});
            skLineSegment(sketch, "E35.0.15.12", {"start": v(-10.38, 1201.74) * mm, "end": v(-10.38, 1198.56) * mm});
            skLineSegment(sketch, "E35.0.15.13", {"start": v(-10.38, 1182.69) * mm, "end": v(-10.38, 1179.51) * mm});
            skLineSegment(sketch, "E35.0.15.14", {"start": v(-19.9, 1182.69) * mm, "end": v(-19.9, 1179.51) * mm});
            skPoint(sketch, "E35.0.16.0", {"position": v(-15.14, 1276.35) * mm});
            skArc(sketch, "E35.0.16.1", {"start": v(-10.38, 1277.94) * mm, "mid": v(-15.14, 1282.7) * mm, "end": v(-19.9, 1277.94) * mm});
            skPoint(sketch, "E35.0.16.2", {"position": v(-15.14, 1257.3) * mm});
            skPoint(sketch, "E35.0.16.3", {"position": v(-15.14, 1238.25) * mm});
            skArc(sketch, "E35.0.16.4", {"start": v(-19.9, 1274.76) * mm, "mid": v(-15.14, 1270) * mm, "end": v(-10.38, 1274.76) * mm});
            skCircle(sketch, "E35.0.16.5", {"center": v(-15.14, 1238.25) * mm, "radius": 4.76 * mm});
            skCircle(sketch, "E35.0.16.6", {"center": v(-15.14, 1219.2) * mm, "radius": 4.76 * mm});
            skArc(sketch, "E35.0.16.7", {"start": v(-10.38, 1258.89) * mm, "mid": v(-15.14, 1263.65) * mm, "end": v(-19.9, 1258.89) * mm});
            skArc(sketch, "E35.0.16.8", {"start": v(-19.9, 1255.71) * mm, "mid": v(-15.14, 1250.95) * mm, "end": v(-10.38, 1255.71) * mm});
            skPoint(sketch, "E35.0.16.9", {"position": v(-15.14, 1276.35) * mm});
            skPoint(sketch, "E35.0.16.10", {"position": v(-15.14, 1257.3) * mm});
            skLineSegment(sketch, "E35.0.16.11", {"start": v(-19.9, 1277.94) * mm, "end": v(-19.9, 1274.76) * mm});
            skLineSegment(sketch, "E35.0.16.12", {"start": v(-10.38, 1277.94) * mm, "end": v(-10.38, 1274.76) * mm});
            skLineSegment(sketch, "E35.0.16.13", {"start": v(-10.38, 1258.89) * mm, "end": v(-10.38, 1255.71) * mm});
            skLineSegment(sketch, "E35.0.16.14", {"start": v(-19.9, 1258.89) * mm, "end": v(-19.9, 1255.71) * mm});
            skPoint(sketch, "E35.0.17.0", {"position": v(-15.14, 1352.55) * mm});
            skArc(sketch, "E35.0.17.1", {"start": v(-10.38, 1354.14) * mm, "mid": v(-15.14, 1358.9) * mm, "end": v(-19.9, 1354.14) * mm});
            skPoint(sketch, "E35.0.17.2", {"position": v(-15.14, 1333.5) * mm});
            skPoint(sketch, "E35.0.17.3", {"position": v(-15.14, 1314.45) * mm});
            skArc(sketch, "E35.0.17.4", {"start": v(-19.9, 1350.96) * mm, "mid": v(-15.14, 1346.2) * mm, "end": v(-10.38, 1350.96) * mm});
            skCircle(sketch, "E35.0.17.5", {"center": v(-15.14, 1314.45) * mm, "radius": 4.76 * mm});
            skCircle(sketch, "E35.0.17.6", {"center": v(-15.14, 1295.4) * mm, "radius": 4.76 * mm});
            skArc(sketch, "E35.0.17.7", {"start": v(-10.38, 1335.09) * mm, "mid": v(-15.14, 1339.85) * mm, "end": v(-19.9, 1335.09) * mm});
            skArc(sketch, "E35.0.17.8", {"start": v(-19.9, 1331.91) * mm, "mid": v(-15.14, 1327.15) * mm, "end": v(-10.38, 1331.91) * mm});
            skPoint(sketch, "E35.0.17.9", {"position": v(-15.14, 1352.55) * mm});
            skPoint(sketch, "E35.0.17.10", {"position": v(-15.14, 1333.5) * mm});
            skLineSegment(sketch, "E35.0.17.11", {"start": v(-19.9, 1354.14) * mm, "end": v(-19.9, 1350.96) * mm});
            skLineSegment(sketch, "E35.0.17.12", {"start": v(-10.38, 1354.14) * mm, "end": v(-10.38, 1350.96) * mm});
            skLineSegment(sketch, "E35.0.17.13", {"start": v(-10.38, 1335.09) * mm, "end": v(-10.38, 1331.91) * mm});
            skLineSegment(sketch, "E35.0.17.14", {"start": v(-19.9, 1335.09) * mm, "end": v(-19.9, 1331.91) * mm});
            skPoint(sketch, "E35.0.18.0", {"position": v(-15.14, 1428.75) * mm});
            skArc(sketch, "E35.0.18.1", {"start": v(-10.38, 1430.34) * mm, "mid": v(-15.14, 1435.1) * mm, "end": v(-19.9, 1430.34) * mm});
            skPoint(sketch, "E35.0.18.2", {"position": v(-15.14, 1409.7) * mm});
            skPoint(sketch, "E35.0.18.3", {"position": v(-15.14, 1390.65) * mm});
            skArc(sketch, "E35.0.18.4", {"start": v(-19.9, 1427.16) * mm, "mid": v(-15.14, 1422.4) * mm, "end": v(-10.38, 1427.16) * mm});
            skCircle(sketch, "E35.0.18.5", {"center": v(-15.14, 1390.65) * mm, "radius": 4.76 * mm});
            skCircle(sketch, "E35.0.18.6", {"center": v(-15.14, 1371.6) * mm, "radius": 4.76 * mm});
            skArc(sketch, "E35.0.18.7", {"start": v(-10.38, 1411.29) * mm, "mid": v(-15.14, 1416.05) * mm, "end": v(-19.9, 1411.29) * mm});
            skArc(sketch, "E35.0.18.8", {"start": v(-19.9, 1408.11) * mm, "mid": v(-15.14, 1403.35) * mm, "end": v(-10.38, 1408.11) * mm});
            skPoint(sketch, "E35.0.18.9", {"position": v(-15.14, 1428.75) * mm});
            skPoint(sketch, "E35.0.18.10", {"position": v(-15.14, 1409.7) * mm});
            skLineSegment(sketch, "E35.0.18.11", {"start": v(-19.9, 1430.34) * mm, "end": v(-19.9, 1427.16) * mm});
            skLineSegment(sketch, "E35.0.18.12", {"start": v(-10.38, 1430.34) * mm, "end": v(-10.38, 1427.16) * mm});
            skLineSegment(sketch, "E35.0.18.13", {"start": v(-10.38, 1411.29) * mm, "end": v(-10.38, 1408.11) * mm});
            skLineSegment(sketch, "E35.0.18.14", {"start": v(-19.9, 1411.29) * mm, "end": v(-19.9, 1408.11) * mm});
            skPoint(sketch, "E35.0.19.0", {"position": v(-15.14, 1504.95) * mm});
            skArc(sketch, "E35.0.19.1", {"start": v(-10.38, 1506.54) * mm, "mid": v(-15.14, 1511.3) * mm, "end": v(-19.9, 1506.54) * mm});
            skPoint(sketch, "E35.0.19.2", {"position": v(-15.14, 1485.9) * mm});
            skPoint(sketch, "E35.0.19.3", {"position": v(-15.14, 1466.85) * mm});
            skArc(sketch, "E35.0.19.4", {"start": v(-19.9, 1503.36) * mm, "mid": v(-15.14, 1498.6) * mm, "end": v(-10.38, 1503.36) * mm});
            skCircle(sketch, "E35.0.19.5", {"center": v(-15.14, 1466.85) * mm, "radius": 4.76 * mm});
            skCircle(sketch, "E35.0.19.6", {"center": v(-15.14, 1447.8) * mm, "radius": 4.76 * mm});
            skArc(sketch, "E35.0.19.7", {"start": v(-10.38, 1487.49) * mm, "mid": v(-15.14, 1492.25) * mm, "end": v(-19.9, 1487.49) * mm});
            skArc(sketch, "E35.0.19.8", {"start": v(-19.9, 1484.31) * mm, "mid": v(-15.14, 1479.55) * mm, "end": v(-10.38, 1484.31) * mm});
            skPoint(sketch, "E35.0.19.9", {"position": v(-15.14, 1504.95) * mm});
            skPoint(sketch, "E35.0.19.10", {"position": v(-15.14, 1485.9) * mm});
            skLineSegment(sketch, "E35.0.19.11", {"start": v(-19.9, 1506.54) * mm, "end": v(-19.9, 1503.36) * mm});
            skLineSegment(sketch, "E35.0.19.12", {"start": v(-10.38, 1506.54) * mm, "end": v(-10.38, 1503.36) * mm});
            skLineSegment(sketch, "E35.0.19.13", {"start": v(-10.38, 1487.49) * mm, "end": v(-10.38, 1484.31) * mm});
            skLineSegment(sketch, "E35.0.19.14", {"start": v(-19.9, 1487.49) * mm, "end": v(-19.9, 1484.31) * mm});
            skPoint(sketch, "E35.0.20.0", {"position": v(-15.14, 1581.15) * mm});
            skArc(sketch, "E35.0.20.1", {"start": v(-10.38, 1582.74) * mm, "mid": v(-15.14, 1587.5) * mm, "end": v(-19.9, 1582.74) * mm});
            skPoint(sketch, "E35.0.20.2", {"position": v(-15.14, 1562.1) * mm});
            skPoint(sketch, "E35.0.20.3", {"position": v(-15.14, 1543.05) * mm});
            skArc(sketch, "E35.0.20.4", {"start": v(-19.9, 1579.56) * mm, "mid": v(-15.14, 1574.8) * mm, "end": v(-10.38, 1579.56) * mm});
            skCircle(sketch, "E35.0.20.5", {"center": v(-15.14, 1543.05) * mm, "radius": 4.76 * mm});
            skCircle(sketch, "E35.0.20.6", {"center": v(-15.14, 1524) * mm, "radius": 4.76 * mm});
            skArc(sketch, "E35.0.20.7", {"start": v(-10.38, 1563.69) * mm, "mid": v(-15.14, 1568.45) * mm, "end": v(-19.9, 1563.69) * mm});
            skArc(sketch, "E35.0.20.8", {"start": v(-19.9, 1560.51) * mm, "mid": v(-15.14, 1555.75) * mm, "end": v(-10.38, 1560.51) * mm});
            skPoint(sketch, "E35.0.20.9", {"position": v(-15.14, 1581.15) * mm});
            skPoint(sketch, "E35.0.20.10", {"position": v(-15.14, 1562.1) * mm});
            skLineSegment(sketch, "E35.0.20.11", {"start": v(-19.9, 1582.74) * mm, "end": v(-19.9, 1579.56) * mm});
            skLineSegment(sketch, "E35.0.20.12", {"start": v(-10.38, 1582.74) * mm, "end": v(-10.38, 1579.56) * mm});
            skLineSegment(sketch, "E35.0.20.13", {"start": v(-10.38, 1563.69) * mm, "end": v(-10.38, 1560.51) * mm});
            skLineSegment(sketch, "E35.0.20.14", {"start": v(-19.9, 1563.69) * mm, "end": v(-19.9, 1560.51) * mm});
            skPoint(sketch, "E35.0.21.0", {"position": v(-15.14, 1657.35) * mm});
            skArc(sketch, "E35.0.21.1", {"start": v(-10.38, 1658.94) * mm, "mid": v(-15.14, 1663.7) * mm, "end": v(-19.9, 1658.94) * mm});
            skPoint(sketch, "E35.0.21.2", {"position": v(-15.14, 1638.3) * mm});
            skPoint(sketch, "E35.0.21.3", {"position": v(-15.14, 1619.25) * mm});
            skArc(sketch, "E35.0.21.4", {"start": v(-19.9, 1655.76) * mm, "mid": v(-15.14, 1651) * mm, "end": v(-10.38, 1655.76) * mm});
            skCircle(sketch, "E35.0.21.5", {"center": v(-15.14, 1619.25) * mm, "radius": 4.76 * mm});
            skCircle(sketch, "E35.0.21.6", {"center": v(-15.14, 1600.2) * mm, "radius": 4.76 * mm});
            skArc(sketch, "E35.0.21.7", {"start": v(-10.38, 1639.89) * mm, "mid": v(-15.14, 1644.65) * mm, "end": v(-19.9, 1639.89) * mm});
            skArc(sketch, "E35.0.21.8", {"start": v(-19.9, 1636.71) * mm, "mid": v(-15.14, 1631.95) * mm, "end": v(-10.38, 1636.71) * mm});
            skPoint(sketch, "E35.0.21.9", {"position": v(-15.14, 1657.35) * mm});
            skPoint(sketch, "E35.0.21.10", {"position": v(-15.14, 1638.3) * mm});
            skLineSegment(sketch, "E35.0.21.11", {"start": v(-19.9, 1658.94) * mm, "end": v(-19.9, 1655.76) * mm});
            skLineSegment(sketch, "E35.0.21.12", {"start": v(-10.38, 1658.94) * mm, "end": v(-10.38, 1655.76) * mm});
            skLineSegment(sketch, "E35.0.21.13", {"start": v(-10.38, 1639.89) * mm, "end": v(-10.38, 1636.71) * mm});
            skLineSegment(sketch, "E35.0.21.14", {"start": v(-19.9, 1639.89) * mm, "end": v(-19.9, 1636.71) * mm});
            skPoint(sketch, "E35.0.22.0", {"position": v(-15.14, 1733.55) * mm});
            skArc(sketch, "E35.0.22.1", {"start": v(-10.38, 1735.14) * mm, "mid": v(-15.14, 1739.9) * mm, "end": v(-19.9, 1735.14) * mm});
            skPoint(sketch, "E35.0.22.2", {"position": v(-15.14, 1714.5) * mm});
            skPoint(sketch, "E35.0.22.3", {"position": v(-15.14, 1695.45) * mm});
            skArc(sketch, "E35.0.22.4", {"start": v(-19.9, 1731.96) * mm, "mid": v(-15.14, 1727.2) * mm, "end": v(-10.38, 1731.96) * mm});
            skCircle(sketch, "E35.0.22.5", {"center": v(-15.14, 1695.45) * mm, "radius": 4.76 * mm});
            skCircle(sketch, "E35.0.22.6", {"center": v(-15.14, 1676.4) * mm, "radius": 4.76 * mm});
            skArc(sketch, "E35.0.22.7", {"start": v(-10.38, 1716.09) * mm, "mid": v(-15.14, 1720.85) * mm, "end": v(-19.9, 1716.09) * mm});
            skArc(sketch, "E35.0.22.8", {"start": v(-19.9, 1712.91) * mm, "mid": v(-15.14, 1708.15) * mm, "end": v(-10.38, 1712.91) * mm});
            skPoint(sketch, "E35.0.22.9", {"position": v(-15.14, 1733.55) * mm});
            skPoint(sketch, "E35.0.22.10", {"position": v(-15.14, 1714.5) * mm});
            skLineSegment(sketch, "E35.0.22.11", {"start": v(-19.9, 1735.14) * mm, "end": v(-19.9, 1731.96) * mm});
            skLineSegment(sketch, "E35.0.22.12", {"start": v(-10.38, 1735.14) * mm, "end": v(-10.38, 1731.96) * mm});
            skLineSegment(sketch, "E35.0.22.13", {"start": v(-10.38, 1716.09) * mm, "end": v(-10.38, 1712.91) * mm});
            skLineSegment(sketch, "E35.0.22.14", {"start": v(-19.9, 1716.09) * mm, "end": v(-19.9, 1712.91) * mm});
            skPoint(sketch, "E35.0.23.0", {"position": v(-15.14, 1809.75) * mm});
            skArc(sketch, "E35.0.23.1", {"start": v(-10.38, 1811.34) * mm, "mid": v(-15.14, 1816.1) * mm, "end": v(-19.9, 1811.34) * mm});
            skPoint(sketch, "E35.0.23.2", {"position": v(-15.14, 1790.7) * mm});
            skPoint(sketch, "E35.0.23.3", {"position": v(-15.14, 1771.65) * mm});
            skArc(sketch, "E35.0.23.4", {"start": v(-19.9, 1808.16) * mm, "mid": v(-15.14, 1803.4) * mm, "end": v(-10.38, 1808.16) * mm});
            skCircle(sketch, "E35.0.23.5", {"center": v(-15.14, 1771.65) * mm, "radius": 4.76 * mm});
            skCircle(sketch, "E35.0.23.6", {"center": v(-15.14, 1752.6) * mm, "radius": 4.76 * mm});
            skArc(sketch, "E35.0.23.7", {"start": v(-10.38, 1792.29) * mm, "mid": v(-15.14, 1797.05) * mm, "end": v(-19.9, 1792.29) * mm});
            skArc(sketch, "E35.0.23.8", {"start": v(-19.9, 1789.11) * mm, "mid": v(-15.14, 1784.35) * mm, "end": v(-10.38, 1789.11) * mm});
            skPoint(sketch, "E35.0.23.9", {"position": v(-15.14, 1809.75) * mm});
            skPoint(sketch, "E35.0.23.10", {"position": v(-15.14, 1790.7) * mm});
            skLineSegment(sketch, "E35.0.23.11", {"start": v(-19.9, 1811.34) * mm, "end": v(-19.9, 1808.16) * mm});
            skLineSegment(sketch, "E35.0.23.12", {"start": v(-10.38, 1811.34) * mm, "end": v(-10.38, 1808.16) * mm});
            skLineSegment(sketch, "E35.0.23.13", {"start": v(-10.38, 1792.29) * mm, "end": v(-10.38, 1789.11) * mm});
            skLineSegment(sketch, "E35.0.23.14", {"start": v(-19.9, 1792.29) * mm, "end": v(-19.9, 1789.11) * mm});
            skLineSegment(sketch, "E35.direction1", {"start": v(-15.14, 0) * mm, "end": v(10.99, 0) * mm, "construction": true});
            skLineSegment(sketch, "E35.direction2", {"start": v(-15.14, 0) * mm, "end": v(-15.14, 76.2) * mm, "construction": true});
            skSolve(sketch);
        }
        {
            var Q0;
            Q0=qSketchRegion(id+"F3",true);
            extrude(context, id + "F5", {"entities" : qUnion([Q0]), "operationType" : NewBodyOperationType.REMOVE, "endBound" : BoundingType.THROUGH_ALL, "oppositeDirection" : true, "depth" : 25.4 * mm, "offsetDistance" : 25.4 * mm});
        }
        {
            var Q0;
            Q0=qSketchRegion(id+"F4",true);
            extrude(context, id + "F6", {"entities" : qUnion([Q0]), "operationType" : NewBodyOperationType.REMOVE, "endBound" : BoundingType.THROUGH_ALL, "oppositeDirection" : true, "depth" : 25.4 * mm, "offsetDistance" : 25.4 * mm});
        }
        {
            var Q0;
            Q0=makeQuery(id+"F2.opExtrude","SWEPT_FACE",FACE,{"disambiguationData":[OSD([sQuery(id+"F1.wireOp",EDGE,"E1")])]});
            var sketch = newSketch(context, id + "F7", { "sketchPlane" : qUnion([Q0])});
            skLineSegment(sketch, "E36", {"start": v(-15.14, 196.85) * mm, "end": v(-15.14, 184.15) * mm, "construction": true});
            skPoint(sketch, "E37", {"position": v(-15.14, 190.5) * mm});
            skSolve(sketch);
        }
        {
            var Q0;
            Q0=makeQuery(id+"F2.opExtrude","SWEPT_FACE",FACE,{"disambiguationData":[OSD([sQuery(id+"F1.wireOp",EDGE,"E0")])]});
            var sketch = newSketch(context, id + "F8", { "sketchPlane" : qUnion([Q0])});
            skLineSegment(sketch, "E38", {"start": v(19.9, 190.5) * mm, "end": v(10.38, 190.5) * mm, "construction": true});
            skPoint(sketch, "E39", {"position": v(15.14, 190.5) * mm});
            skSolve(sketch);
        }
    });
